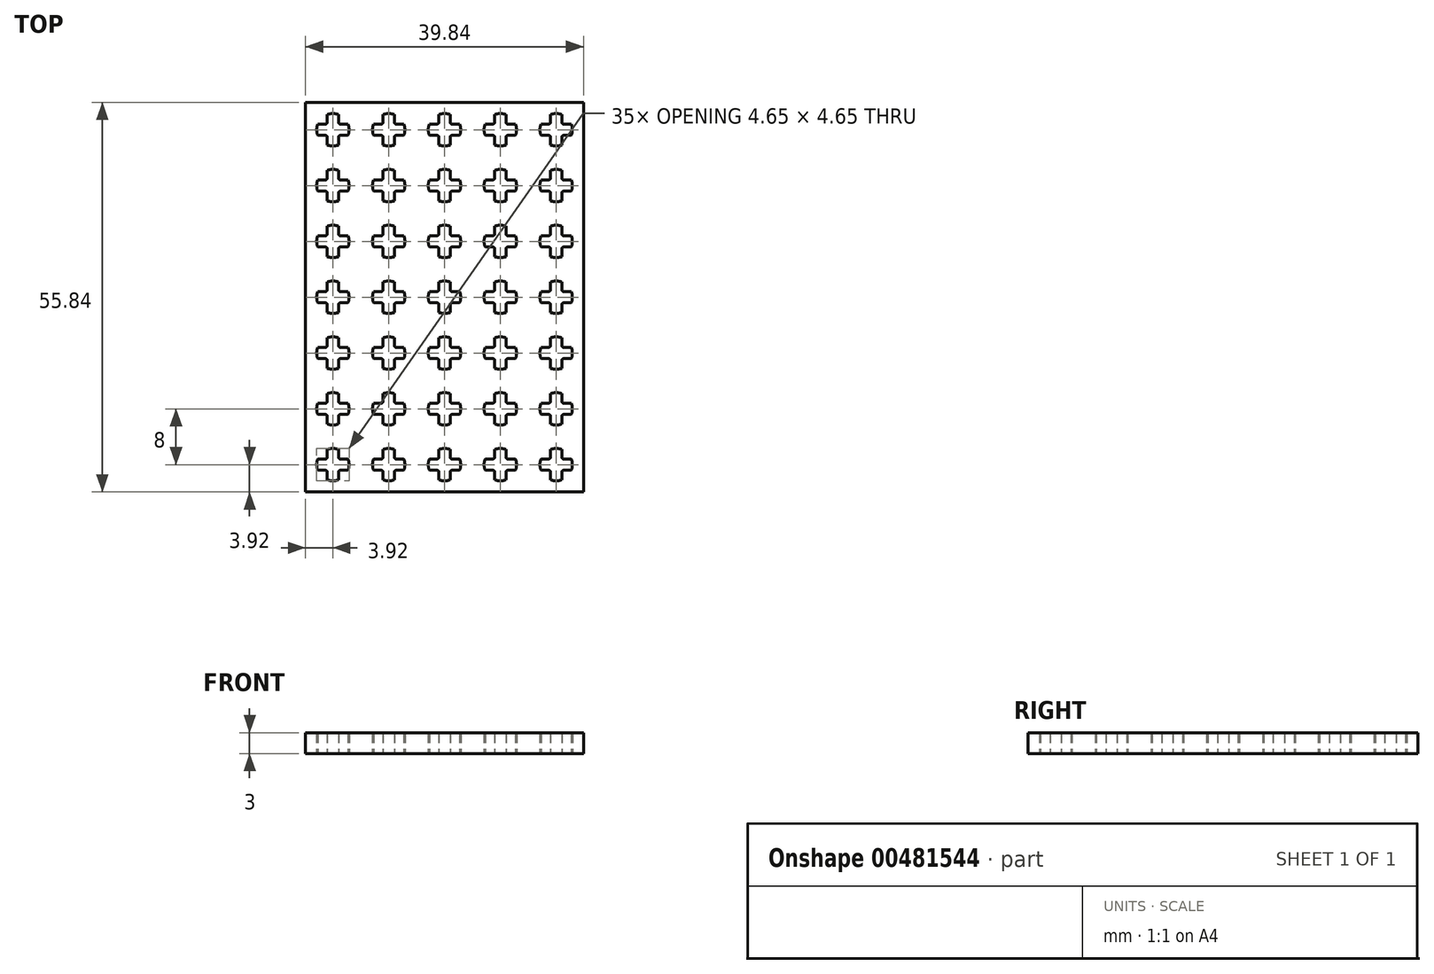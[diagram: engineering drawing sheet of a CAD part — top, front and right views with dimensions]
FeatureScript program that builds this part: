
annotation { "Feature Type Name" : "Feature", "Feature Type Description" : "" }
export const myFeature = defineFeature(function(context is Context, id is Id, definition is map)
    precondition{}
    {
        {
            var Q0;
            Q0=qCreatedBy(makeId("Top.planeOp"),FACE);
            var sketch = newSketch(context, id + "F0", { "sketchPlane" : qUnion([Q0])});
            skLineSegment(sketch, "E0.bottom", {"start": v(-20, 28) * mm, "end": v(20, 28) * mm, "construction": true});
            skLineSegment(sketch, "E0.top", {"start": v(-20, -28) * mm, "end": v(20, -28) * mm, "construction": true});
            skLineSegment(sketch, "E0.left", {"start": v(-20, 28) * mm, "end": v(-20, -28) * mm, "construction": true});
            skLineSegment(sketch, "E0.right", {"start": v(20, 28) * mm, "end": v(20, -28) * mm, "construction": true});
            skLineSegment(sketch, "E1", {"start": v(-16.8, 26.18) * mm, "end": v(-15.2, 26.18) * mm, "construction": true});
            skLineSegment(sketch, "E2", {"start": v(-15.2, 26.18) * mm, "end": v(-15.2, 25.1) * mm});
            skLineSegment(sketch, "E3", {"start": v(-14.9, 24.8) * mm, "end": v(-13.82, 24.8) * mm});
            skLineSegment(sketch, "E4", {"start": v(-13.82, 24.8) * mm, "end": v(-16, 24) * mm, "construction": true});
            skLineSegment(sketch, "E5", {"start": v(-16, 24) * mm, "end": v(-16.8, 26.18) * mm, "construction": true});
            skArc(sketch, "E6", {"start": v(-15.2, 26.18) * mm, "mid": v(-16, 26.33) * mm, "end": v(-16.8, 26.18) * mm});
            skArc(sketch, "E7", {"start": v(-15.2, 25.1) * mm, "mid": v(-15.11, 24.89) * mm, "end": v(-14.9, 24.8) * mm});
            skLineSegment(sketch, "E8", {"start": v(-15.2, 26.18) * mm, "end": v(-15.2, 24.8) * mm, "construction": true});
            skLineSegment(sketch, "E9", {"start": v(-15.2, 24.8) * mm, "end": v(-13.82, 24.8) * mm, "construction": true});
            skArc(sketch, "E10.1.0", {"start": v(-18.18, 24.8) * mm, "mid": v(-18.32, 24) * mm, "end": v(-18.18, 23.2) * mm});
            skArc(sketch, "E10.1.1", {"start": v(-17.1, 24.8) * mm, "mid": v(-16.89, 24.89) * mm, "end": v(-16.8, 25.1) * mm});
            skLineSegment(sketch, "E10.1.2", {"start": v(-18.18, 24.8) * mm, "end": v(-17.1, 24.8) * mm});
            skLineSegment(sketch, "E10.1.3", {"start": v(-16.8, 25.1) * mm, "end": v(-16.8, 26.18) * mm});
            skArc(sketch, "E10.2.0", {"start": v(-16.8, 21.82) * mm, "mid": v(-16, 21.68) * mm, "end": v(-15.2, 21.82) * mm});
            skArc(sketch, "E10.2.1", {"start": v(-16.8, 22.9) * mm, "mid": v(-16.89, 23.11) * mm, "end": v(-17.1, 23.2) * mm});
            skLineSegment(sketch, "E10.2.2", {"start": v(-16.8, 21.82) * mm, "end": v(-16.8, 22.9) * mm});
            skLineSegment(sketch, "E10.2.3", {"start": v(-17.1, 23.2) * mm, "end": v(-18.18, 23.2) * mm});
            skArc(sketch, "E10.3.0", {"start": v(-13.82, 23.2) * mm, "mid": v(-13.67, 24) * mm, "end": v(-13.82, 24.8) * mm});
            skArc(sketch, "E10.3.1", {"start": v(-14.9, 23.2) * mm, "mid": v(-15.11, 23.11) * mm, "end": v(-15.2, 22.9) * mm});
            skLineSegment(sketch, "E10.3.2", {"start": v(-13.82, 23.2) * mm, "end": v(-14.9, 23.2) * mm});
            skLineSegment(sketch, "E10.3.3", {"start": v(-15.2, 22.9) * mm, "end": v(-15.2, 21.82) * mm});
            skLineSegment(sketch, "E11.bottom", {"start": v(-19.92, 27.93) * mm, "end": v(19.93, 27.92) * mm});
            skLineSegment(sketch, "E11.top", {"start": v(-19.93, -27.92) * mm, "end": v(19.92, -27.93) * mm});
            skLineSegment(sketch, "E11.left", {"start": v(-19.92, 27.93) * mm, "end": v(-19.93, -27.92) * mm});
            skLineSegment(sketch, "E11.right", {"start": v(19.93, 27.92) * mm, "end": v(19.92, -27.93) * mm});
            skArc(sketch, "E12.0.1.0", {"start": v(-16.8, 13.82) * mm, "mid": v(-16, 13.67) * mm, "end": v(-15.2, 13.82) * mm});
            skArc(sketch, "E12.0.1.1", {"start": v(-18.18, 16.8) * mm, "mid": v(-18.32, 16) * mm, "end": v(-18.18, 15.2) * mm});
            skArc(sketch, "E12.0.1.2", {"start": v(-15.2, 18.18) * mm, "mid": v(-16, 18.32) * mm, "end": v(-16.8, 18.18) * mm});
            skLineSegment(sketch, "E12.0.1.3", {"start": v(-16.8, 18.18) * mm, "end": v(-15.2, 18.18) * mm, "construction": true});
            skArc(sketch, "E12.0.1.4", {"start": v(-13.82, 15.2) * mm, "mid": v(-13.67, 16) * mm, "end": v(-13.82, 16.8) * mm});
            skPoint(sketch, "E12.0.1.5", {"position": v(-16, 16) * mm});
            skLineSegment(sketch, "E12.0.1.6", {"start": v(-18.18, 16.8) * mm, "end": v(-17.1, 16.8) * mm});
            skLineSegment(sketch, "E12.0.1.7", {"start": v(-17.1, 15.2) * mm, "end": v(-18.18, 15.2) * mm});
            skLineSegment(sketch, "E12.0.1.8", {"start": v(-13.82, 15.2) * mm, "end": v(-14.9, 15.2) * mm});
            skArc(sketch, "E12.0.1.9", {"start": v(-14.9, 15.2) * mm, "mid": v(-15.11, 15.11) * mm, "end": v(-15.2, 14.9) * mm});
            skLineSegment(sketch, "E12.0.1.10", {"start": v(-16, 16) * mm, "end": v(-16.8, 18.18) * mm, "construction": true});
            skLineSegment(sketch, "E12.0.1.11", {"start": v(-16.8, 13.82) * mm, "end": v(-16.8, 14.9) * mm});
            skLineSegment(sketch, "E12.0.1.12", {"start": v(-15.2, 14.9) * mm, "end": v(-15.2, 13.82) * mm});
            skArc(sketch, "E12.0.1.13", {"start": v(-16.8, 14.9) * mm, "mid": v(-16.89, 15.11) * mm, "end": v(-17.1, 15.2) * mm});
            skArc(sketch, "E12.0.1.14", {"start": v(-17.1, 16.8) * mm, "mid": v(-16.89, 16.89) * mm, "end": v(-16.8, 17.1) * mm});
            skLineSegment(sketch, "E12.0.1.15", {"start": v(-16.8, 17.1) * mm, "end": v(-16.8, 18.18) * mm});
            skLineSegment(sketch, "E12.0.1.16", {"start": v(-15.2, 16.8) * mm, "end": v(-13.82, 16.8) * mm, "construction": true});
            skArc(sketch, "E12.0.1.17", {"start": v(-15.2, 17.1) * mm, "mid": v(-15.11, 16.89) * mm, "end": v(-14.9, 16.8) * mm});
            skLineSegment(sketch, "E12.0.1.18", {"start": v(-15.2, 18.18) * mm, "end": v(-15.2, 16.8) * mm, "construction": true});
            skLineSegment(sketch, "E12.0.1.19", {"start": v(-13.82, 16.8) * mm, "end": v(-16, 16) * mm, "construction": true});
            skLineSegment(sketch, "E12.0.1.20", {"start": v(-15.2, 18.18) * mm, "end": v(-15.2, 17.1) * mm});
            skLineSegment(sketch, "E12.0.1.21", {"start": v(-14.9, 16.8) * mm, "end": v(-13.82, 16.8) * mm});
            skArc(sketch, "E12.0.2.0", {"start": v(-16.8, 5.82) * mm, "mid": v(-16, 5.67) * mm, "end": v(-15.2, 5.82) * mm});
            skArc(sketch, "E12.0.2.1", {"start": v(-18.18, 8.8) * mm, "mid": v(-18.32, 8) * mm, "end": v(-18.18, 7.2) * mm});
            skArc(sketch, "E12.0.2.2", {"start": v(-15.2, 10.18) * mm, "mid": v(-16, 10.32) * mm, "end": v(-16.8, 10.18) * mm});
            skLineSegment(sketch, "E12.0.2.3", {"start": v(-16.8, 10.18) * mm, "end": v(-15.2, 10.18) * mm, "construction": true});
            skArc(sketch, "E12.0.2.4", {"start": v(-13.82, 7.2) * mm, "mid": v(-13.67, 8) * mm, "end": v(-13.82, 8.8) * mm});
            skPoint(sketch, "E12.0.2.5", {"position": v(-16, 8) * mm});
            skLineSegment(sketch, "E12.0.2.6", {"start": v(-18.18, 8.8) * mm, "end": v(-17.1, 8.8) * mm});
            skLineSegment(sketch, "E12.0.2.7", {"start": v(-17.1, 7.2) * mm, "end": v(-18.18, 7.2) * mm});
            skLineSegment(sketch, "E12.0.2.8", {"start": v(-13.82, 7.2) * mm, "end": v(-14.9, 7.2) * mm});
            skArc(sketch, "E12.0.2.9", {"start": v(-14.9, 7.2) * mm, "mid": v(-15.11, 7.11) * mm, "end": v(-15.2, 6.9) * mm});
            skLineSegment(sketch, "E12.0.2.10", {"start": v(-16, 8) * mm, "end": v(-16.8, 10.18) * mm, "construction": true});
            skLineSegment(sketch, "E12.0.2.11", {"start": v(-16.8, 5.82) * mm, "end": v(-16.8, 6.9) * mm});
            skLineSegment(sketch, "E12.0.2.12", {"start": v(-15.2, 6.9) * mm, "end": v(-15.2, 5.82) * mm});
            skArc(sketch, "E12.0.2.13", {"start": v(-16.8, 6.9) * mm, "mid": v(-16.89, 7.11) * mm, "end": v(-17.1, 7.2) * mm});
            skArc(sketch, "E12.0.2.14", {"start": v(-17.1, 8.8) * mm, "mid": v(-16.89, 8.89) * mm, "end": v(-16.8, 9.1) * mm});
            skLineSegment(sketch, "E12.0.2.15", {"start": v(-16.8, 9.1) * mm, "end": v(-16.8, 10.18) * mm});
            skLineSegment(sketch, "E12.0.2.16", {"start": v(-15.2, 8.8) * mm, "end": v(-13.82, 8.8) * mm, "construction": true});
            skArc(sketch, "E12.0.2.17", {"start": v(-15.2, 9.1) * mm, "mid": v(-15.11, 8.89) * mm, "end": v(-14.9, 8.8) * mm});
            skLineSegment(sketch, "E12.0.2.18", {"start": v(-15.2, 10.18) * mm, "end": v(-15.2, 8.8) * mm, "construction": true});
            skLineSegment(sketch, "E12.0.2.19", {"start": v(-13.82, 8.8) * mm, "end": v(-16, 8) * mm, "construction": true});
            skLineSegment(sketch, "E12.0.2.20", {"start": v(-15.2, 10.18) * mm, "end": v(-15.2, 9.1) * mm});
            skLineSegment(sketch, "E12.0.2.21", {"start": v(-14.9, 8.8) * mm, "end": v(-13.82, 8.8) * mm});
            skArc(sketch, "E12.0.3.0", {"start": v(-16.8, -2.18) * mm, "mid": v(-16, -2.33) * mm, "end": v(-15.2, -2.18) * mm});
            skArc(sketch, "E12.0.3.1", {"start": v(-18.18, 0.8) * mm, "mid": v(-18.32, 0) * mm, "end": v(-18.18, -0.8) * mm});
            skArc(sketch, "E12.0.3.2", {"start": v(-15.2, 2.18) * mm, "mid": v(-16, 2.32) * mm, "end": v(-16.8, 2.18) * mm});
            skLineSegment(sketch, "E12.0.3.3", {"start": v(-16.8, 2.18) * mm, "end": v(-15.2, 2.18) * mm, "construction": true});
            skArc(sketch, "E12.0.3.4", {"start": v(-13.82, -0.8) * mm, "mid": v(-13.67, 0) * mm, "end": v(-13.82, 0.8) * mm});
            skPoint(sketch, "E12.0.3.5", {"position": v(-16, 0) * mm});
            skLineSegment(sketch, "E12.0.3.6", {"start": v(-18.18, 0.8) * mm, "end": v(-17.1, 0.8) * mm});
            skLineSegment(sketch, "E12.0.3.7", {"start": v(-17.1, -0.8) * mm, "end": v(-18.18, -0.8) * mm});
            skLineSegment(sketch, "E12.0.3.8", {"start": v(-13.82, -0.8) * mm, "end": v(-14.9, -0.8) * mm});
            skArc(sketch, "E12.0.3.9", {"start": v(-14.9, -0.8) * mm, "mid": v(-15.11, -0.89) * mm, "end": v(-15.2, -1.1) * mm});
            skLineSegment(sketch, "E12.0.3.10", {"start": v(-16, 0) * mm, "end": v(-16.8, 2.18) * mm, "construction": true});
            skLineSegment(sketch, "E12.0.3.11", {"start": v(-16.8, -2.18) * mm, "end": v(-16.8, -1.1) * mm});
            skLineSegment(sketch, "E12.0.3.12", {"start": v(-15.2, -1.1) * mm, "end": v(-15.2, -2.18) * mm});
            skArc(sketch, "E12.0.3.13", {"start": v(-16.8, -1.1) * mm, "mid": v(-16.89, -0.89) * mm, "end": v(-17.1, -0.8) * mm});
            skArc(sketch, "E12.0.3.14", {"start": v(-17.1, 0.8) * mm, "mid": v(-16.89, 0.89) * mm, "end": v(-16.8, 1.1) * mm});
            skLineSegment(sketch, "E12.0.3.15", {"start": v(-16.8, 1.1) * mm, "end": v(-16.8, 2.18) * mm});
            skLineSegment(sketch, "E12.0.3.16", {"start": v(-15.2, 0.8) * mm, "end": v(-13.82, 0.8) * mm, "construction": true});
            skArc(sketch, "E12.0.3.17", {"start": v(-15.2, 1.1) * mm, "mid": v(-15.11, 0.89) * mm, "end": v(-14.9, 0.8) * mm});
            skLineSegment(sketch, "E12.0.3.18", {"start": v(-15.2, 2.18) * mm, "end": v(-15.2, 0.8) * mm, "construction": true});
            skLineSegment(sketch, "E12.0.3.19", {"start": v(-13.82, 0.8) * mm, "end": v(-16, 0) * mm, "construction": true});
            skLineSegment(sketch, "E12.0.3.20", {"start": v(-15.2, 2.18) * mm, "end": v(-15.2, 1.1) * mm});
            skLineSegment(sketch, "E12.0.3.21", {"start": v(-14.9, 0.8) * mm, "end": v(-13.82, 0.8) * mm});
            skArc(sketch, "E12.0.4.0", {"start": v(-16.8, -10.18) * mm, "mid": v(-16, -10.33) * mm, "end": v(-15.2, -10.18) * mm});
            skArc(sketch, "E12.0.4.1", {"start": v(-18.18, -7.2) * mm, "mid": v(-18.32, -8) * mm, "end": v(-18.18, -8.8) * mm});
            skArc(sketch, "E12.0.4.2", {"start": v(-15.2, -5.82) * mm, "mid": v(-16, -5.68) * mm, "end": v(-16.8, -5.82) * mm});
            skLineSegment(sketch, "E12.0.4.3", {"start": v(-16.8, -5.82) * mm, "end": v(-15.2, -5.82) * mm, "construction": true});
            skArc(sketch, "E12.0.4.4", {"start": v(-13.82, -8.8) * mm, "mid": v(-13.67, -8) * mm, "end": v(-13.82, -7.2) * mm});
            skPoint(sketch, "E12.0.4.5", {"position": v(-16, -8) * mm});
            skLineSegment(sketch, "E12.0.4.6", {"start": v(-18.18, -7.2) * mm, "end": v(-17.1, -7.2) * mm});
            skLineSegment(sketch, "E12.0.4.7", {"start": v(-17.1, -8.8) * mm, "end": v(-18.18, -8.8) * mm});
            skLineSegment(sketch, "E12.0.4.8", {"start": v(-13.82, -8.8) * mm, "end": v(-14.9, -8.8) * mm});
            skArc(sketch, "E12.0.4.9", {"start": v(-14.9, -8.8) * mm, "mid": v(-15.11, -8.89) * mm, "end": v(-15.2, -9.1) * mm});
            skLineSegment(sketch, "E12.0.4.10", {"start": v(-16, -8) * mm, "end": v(-16.8, -5.82) * mm, "construction": true});
            skLineSegment(sketch, "E12.0.4.11", {"start": v(-16.8, -10.18) * mm, "end": v(-16.8, -9.1) * mm});
            skLineSegment(sketch, "E12.0.4.12", {"start": v(-15.2, -9.1) * mm, "end": v(-15.2, -10.18) * mm});
            skArc(sketch, "E12.0.4.13", {"start": v(-16.8, -9.1) * mm, "mid": v(-16.89, -8.89) * mm, "end": v(-17.1, -8.8) * mm});
            skArc(sketch, "E12.0.4.14", {"start": v(-17.1, -7.2) * mm, "mid": v(-16.89, -7.11) * mm, "end": v(-16.8, -6.9) * mm});
            skLineSegment(sketch, "E12.0.4.15", {"start": v(-16.8, -6.9) * mm, "end": v(-16.8, -5.82) * mm});
            skLineSegment(sketch, "E12.0.4.16", {"start": v(-15.2, -7.2) * mm, "end": v(-13.82, -7.2) * mm, "construction": true});
            skArc(sketch, "E12.0.4.17", {"start": v(-15.2, -6.9) * mm, "mid": v(-15.11, -7.11) * mm, "end": v(-14.9, -7.2) * mm});
            skLineSegment(sketch, "E12.0.4.18", {"start": v(-15.2, -5.82) * mm, "end": v(-15.2, -7.2) * mm, "construction": true});
            skLineSegment(sketch, "E12.0.4.19", {"start": v(-13.82, -7.2) * mm, "end": v(-16, -8) * mm, "construction": true});
            skLineSegment(sketch, "E12.0.4.20", {"start": v(-15.2, -5.82) * mm, "end": v(-15.2, -6.9) * mm});
            skLineSegment(sketch, "E12.0.4.21", {"start": v(-14.9, -7.2) * mm, "end": v(-13.82, -7.2) * mm});
            skArc(sketch, "E12.0.5.0", {"start": v(-16.8, -18.18) * mm, "mid": v(-16, -18.33) * mm, "end": v(-15.2, -18.18) * mm});
            skArc(sketch, "E12.0.5.1", {"start": v(-18.18, -15.2) * mm, "mid": v(-18.32, -16) * mm, "end": v(-18.18, -16.8) * mm});
            skArc(sketch, "E12.0.5.2", {"start": v(-15.2, -13.82) * mm, "mid": v(-16, -13.68) * mm, "end": v(-16.8, -13.82) * mm});
            skLineSegment(sketch, "E12.0.5.3", {"start": v(-16.8, -13.82) * mm, "end": v(-15.2, -13.82) * mm, "construction": true});
            skArc(sketch, "E12.0.5.4", {"start": v(-13.82, -16.8) * mm, "mid": v(-13.67, -16) * mm, "end": v(-13.82, -15.2) * mm});
            skPoint(sketch, "E12.0.5.5", {"position": v(-16, -16) * mm});
            skLineSegment(sketch, "E12.0.5.6", {"start": v(-18.18, -15.2) * mm, "end": v(-17.1, -15.2) * mm});
            skLineSegment(sketch, "E12.0.5.7", {"start": v(-17.1, -16.8) * mm, "end": v(-18.18, -16.8) * mm});
            skLineSegment(sketch, "E12.0.5.8", {"start": v(-13.82, -16.8) * mm, "end": v(-14.9, -16.8) * mm});
            skArc(sketch, "E12.0.5.9", {"start": v(-14.9, -16.8) * mm, "mid": v(-15.11, -16.89) * mm, "end": v(-15.2, -17.1) * mm});
            skLineSegment(sketch, "E12.0.5.10", {"start": v(-16, -16) * mm, "end": v(-16.8, -13.82) * mm, "construction": true});
            skLineSegment(sketch, "E12.0.5.11", {"start": v(-16.8, -18.18) * mm, "end": v(-16.8, -17.1) * mm});
            skLineSegment(sketch, "E12.0.5.12", {"start": v(-15.2, -17.1) * mm, "end": v(-15.2, -18.18) * mm});
            skArc(sketch, "E12.0.5.13", {"start": v(-16.8, -17.1) * mm, "mid": v(-16.89, -16.89) * mm, "end": v(-17.1, -16.8) * mm});
            skArc(sketch, "E12.0.5.14", {"start": v(-17.1, -15.2) * mm, "mid": v(-16.89, -15.11) * mm, "end": v(-16.8, -14.9) * mm});
            skLineSegment(sketch, "E12.0.5.15", {"start": v(-16.8, -14.9) * mm, "end": v(-16.8, -13.82) * mm});
            skLineSegment(sketch, "E12.0.5.16", {"start": v(-15.2, -15.2) * mm, "end": v(-13.82, -15.2) * mm, "construction": true});
            skArc(sketch, "E12.0.5.17", {"start": v(-15.2, -14.9) * mm, "mid": v(-15.11, -15.11) * mm, "end": v(-14.9, -15.2) * mm});
            skLineSegment(sketch, "E12.0.5.18", {"start": v(-15.2, -13.82) * mm, "end": v(-15.2, -15.2) * mm, "construction": true});
            skLineSegment(sketch, "E12.0.5.19", {"start": v(-13.82, -15.2) * mm, "end": v(-16, -16) * mm, "construction": true});
            skLineSegment(sketch, "E12.0.5.20", {"start": v(-15.2, -13.82) * mm, "end": v(-15.2, -14.9) * mm});
            skLineSegment(sketch, "E12.0.5.21", {"start": v(-14.9, -15.2) * mm, "end": v(-13.82, -15.2) * mm});
            skArc(sketch, "E12.0.6.0", {"start": v(-16.8, -26.18) * mm, "mid": v(-16, -26.33) * mm, "end": v(-15.2, -26.18) * mm});
            skArc(sketch, "E12.0.6.1", {"start": v(-18.18, -23.2) * mm, "mid": v(-18.32, -24) * mm, "end": v(-18.18, -24.8) * mm});
            skArc(sketch, "E12.0.6.2", {"start": v(-15.2, -21.82) * mm, "mid": v(-16, -21.68) * mm, "end": v(-16.8, -21.82) * mm});
            skLineSegment(sketch, "E12.0.6.3", {"start": v(-16.8, -21.82) * mm, "end": v(-15.2, -21.82) * mm, "construction": true});
            skArc(sketch, "E12.0.6.4", {"start": v(-13.82, -24.8) * mm, "mid": v(-13.67, -24) * mm, "end": v(-13.82, -23.2) * mm});
            skPoint(sketch, "E12.0.6.5", {"position": v(-16, -24) * mm});
            skLineSegment(sketch, "E12.0.6.6", {"start": v(-18.18, -23.2) * mm, "end": v(-17.1, -23.2) * mm});
            skLineSegment(sketch, "E12.0.6.7", {"start": v(-17.1, -24.8) * mm, "end": v(-18.18, -24.8) * mm});
            skLineSegment(sketch, "E12.0.6.8", {"start": v(-13.82, -24.8) * mm, "end": v(-14.9, -24.8) * mm});
            skArc(sketch, "E12.0.6.9", {"start": v(-14.9, -24.8) * mm, "mid": v(-15.11, -24.89) * mm, "end": v(-15.2, -25.1) * mm});
            skLineSegment(sketch, "E12.0.6.10", {"start": v(-16, -24) * mm, "end": v(-16.8, -21.82) * mm, "construction": true});
            skLineSegment(sketch, "E12.0.6.11", {"start": v(-16.8, -26.18) * mm, "end": v(-16.8, -25.1) * mm});
            skLineSegment(sketch, "E12.0.6.12", {"start": v(-15.2, -25.1) * mm, "end": v(-15.2, -26.18) * mm});
            skArc(sketch, "E12.0.6.13", {"start": v(-16.8, -25.1) * mm, "mid": v(-16.89, -24.89) * mm, "end": v(-17.1, -24.8) * mm});
            skArc(sketch, "E12.0.6.14", {"start": v(-17.1, -23.2) * mm, "mid": v(-16.89, -23.11) * mm, "end": v(-16.8, -22.9) * mm});
            skLineSegment(sketch, "E12.0.6.15", {"start": v(-16.8, -22.9) * mm, "end": v(-16.8, -21.82) * mm});
            skLineSegment(sketch, "E12.0.6.16", {"start": v(-15.2, -23.2) * mm, "end": v(-13.82, -23.2) * mm, "construction": true});
            skArc(sketch, "E12.0.6.17", {"start": v(-15.2, -22.9) * mm, "mid": v(-15.11, -23.11) * mm, "end": v(-14.9, -23.2) * mm});
            skLineSegment(sketch, "E12.0.6.18", {"start": v(-15.2, -21.82) * mm, "end": v(-15.2, -23.2) * mm, "construction": true});
            skLineSegment(sketch, "E12.0.6.19", {"start": v(-13.82, -23.2) * mm, "end": v(-16, -24) * mm, "construction": true});
            skLineSegment(sketch, "E12.0.6.20", {"start": v(-15.2, -21.82) * mm, "end": v(-15.2, -22.9) * mm});
            skLineSegment(sketch, "E12.0.6.21", {"start": v(-14.9, -23.2) * mm, "end": v(-13.82, -23.2) * mm});
            skArc(sketch, "E12.0.7.0", {"start": v(-16.8, -34.18) * mm, "mid": v(-16, -34.33) * mm, "end": v(-15.2, -34.18) * mm});
            skArc(sketch, "E12.0.7.1", {"start": v(-18.18, -31.2) * mm, "mid": v(-18.32, -32) * mm, "end": v(-18.18, -32.8) * mm});
            skArc(sketch, "E12.0.7.2", {"start": v(-15.2, -29.82) * mm, "mid": v(-16, -29.68) * mm, "end": v(-16.8, -29.82) * mm});
            skLineSegment(sketch, "E12.0.7.3", {"start": v(-16.8, -29.82) * mm, "end": v(-15.2, -29.82) * mm, "construction": true});
            skArc(sketch, "E12.0.7.4", {"start": v(-13.82, -32.8) * mm, "mid": v(-13.67, -32) * mm, "end": v(-13.82, -31.2) * mm});
            skPoint(sketch, "E12.0.7.5", {"position": v(-16, -32) * mm});
            skLineSegment(sketch, "E12.0.7.6", {"start": v(-18.18, -31.2) * mm, "end": v(-17.1, -31.2) * mm});
            skLineSegment(sketch, "E12.0.7.7", {"start": v(-17.1, -32.8) * mm, "end": v(-18.18, -32.8) * mm});
            skLineSegment(sketch, "E12.0.7.8", {"start": v(-13.82, -32.8) * mm, "end": v(-14.9, -32.8) * mm});
            skArc(sketch, "E12.0.7.9", {"start": v(-14.9, -32.8) * mm, "mid": v(-15.11, -32.89) * mm, "end": v(-15.2, -33.1) * mm});
            skLineSegment(sketch, "E12.0.7.10", {"start": v(-16, -32) * mm, "end": v(-16.8, -29.82) * mm, "construction": true});
            skLineSegment(sketch, "E12.0.7.11", {"start": v(-16.8, -34.18) * mm, "end": v(-16.8, -33.1) * mm});
            skLineSegment(sketch, "E12.0.7.12", {"start": v(-15.2, -33.1) * mm, "end": v(-15.2, -34.18) * mm});
            skArc(sketch, "E12.0.7.13", {"start": v(-16.8, -33.1) * mm, "mid": v(-16.89, -32.89) * mm, "end": v(-17.1, -32.8) * mm});
            skArc(sketch, "E12.0.7.14", {"start": v(-17.1, -31.2) * mm, "mid": v(-16.89, -31.11) * mm, "end": v(-16.8, -30.9) * mm});
            skLineSegment(sketch, "E12.0.7.15", {"start": v(-16.8, -30.9) * mm, "end": v(-16.8, -29.82) * mm});
            skLineSegment(sketch, "E12.0.7.16", {"start": v(-15.2, -31.2) * mm, "end": v(-13.82, -31.2) * mm, "construction": true});
            skArc(sketch, "E12.0.7.17", {"start": v(-15.2, -30.9) * mm, "mid": v(-15.11, -31.11) * mm, "end": v(-14.9, -31.2) * mm});
            skLineSegment(sketch, "E12.0.7.18", {"start": v(-15.2, -29.82) * mm, "end": v(-15.2, -31.2) * mm, "construction": true});
            skLineSegment(sketch, "E12.0.7.19", {"start": v(-13.82, -31.2) * mm, "end": v(-16, -32) * mm, "construction": true});
            skLineSegment(sketch, "E12.0.7.20", {"start": v(-15.2, -29.82) * mm, "end": v(-15.2, -30.9) * mm});
            skLineSegment(sketch, "E12.0.7.21", {"start": v(-14.9, -31.2) * mm, "end": v(-13.82, -31.2) * mm});
            skArc(sketch, "E12.1.0.0", {"start": v(-8.8, 21.82) * mm, "mid": v(-8, 21.67) * mm, "end": v(-7.2, 21.82) * mm});
            skArc(sketch, "E12.1.0.1", {"start": v(-10.18, 24.8) * mm, "mid": v(-10.33, 24) * mm, "end": v(-10.18, 23.2) * mm});
            skArc(sketch, "E12.1.0.2", {"start": v(-7.2, 26.18) * mm, "mid": v(-8, 26.32) * mm, "end": v(-8.8, 26.18) * mm});
            skLineSegment(sketch, "E12.1.0.3", {"start": v(-8.8, 26.18) * mm, "end": v(-7.2, 26.18) * mm, "construction": true});
            skArc(sketch, "E12.1.0.4", {"start": v(-5.82, 23.2) * mm, "mid": v(-5.67, 24) * mm, "end": v(-5.82, 24.8) * mm});
            skPoint(sketch, "E12.1.0.5", {"position": v(-8, 24) * mm});
            skLineSegment(sketch, "E12.1.0.6", {"start": v(-10.18, 24.8) * mm, "end": v(-9.1, 24.8) * mm});
            skLineSegment(sketch, "E12.1.0.7", {"start": v(-9.1, 23.2) * mm, "end": v(-10.18, 23.2) * mm});
            skLineSegment(sketch, "E12.1.0.8", {"start": v(-5.82, 23.2) * mm, "end": v(-6.9, 23.2) * mm});
            skArc(sketch, "E12.1.0.9", {"start": v(-6.9, 23.2) * mm, "mid": v(-7.11, 23.11) * mm, "end": v(-7.2, 22.9) * mm});
            skLineSegment(sketch, "E12.1.0.10", {"start": v(-8, 24) * mm, "end": v(-8.8, 26.18) * mm, "construction": true});
            skLineSegment(sketch, "E12.1.0.11", {"start": v(-8.8, 21.82) * mm, "end": v(-8.8, 22.9) * mm});
            skLineSegment(sketch, "E12.1.0.12", {"start": v(-7.2, 22.9) * mm, "end": v(-7.2, 21.82) * mm});
            skArc(sketch, "E12.1.0.13", {"start": v(-8.8, 22.9) * mm, "mid": v(-8.89, 23.11) * mm, "end": v(-9.1, 23.2) * mm});
            skArc(sketch, "E12.1.0.14", {"start": v(-9.1, 24.8) * mm, "mid": v(-8.89, 24.89) * mm, "end": v(-8.8, 25.1) * mm});
            skLineSegment(sketch, "E12.1.0.15", {"start": v(-8.8, 25.1) * mm, "end": v(-8.8, 26.18) * mm});
            skLineSegment(sketch, "E12.1.0.16", {"start": v(-7.2, 24.8) * mm, "end": v(-5.82, 24.8) * mm, "construction": true});
            skArc(sketch, "E12.1.0.17", {"start": v(-7.2, 25.1) * mm, "mid": v(-7.11, 24.89) * mm, "end": v(-6.9, 24.8) * mm});
            skLineSegment(sketch, "E12.1.0.18", {"start": v(-7.2, 26.18) * mm, "end": v(-7.2, 24.8) * mm, "construction": true});
            skLineSegment(sketch, "E12.1.0.19", {"start": v(-5.82, 24.8) * mm, "end": v(-8, 24) * mm, "construction": true});
            skLineSegment(sketch, "E12.1.0.20", {"start": v(-7.2, 26.18) * mm, "end": v(-7.2, 25.1) * mm});
            skLineSegment(sketch, "E12.1.0.21", {"start": v(-6.9, 24.8) * mm, "end": v(-5.82, 24.8) * mm});
            skArc(sketch, "E12.1.1.0", {"start": v(-8.8, 13.82) * mm, "mid": v(-8, 13.67) * mm, "end": v(-7.2, 13.82) * mm});
            skArc(sketch, "E12.1.1.1", {"start": v(-10.18, 16.8) * mm, "mid": v(-10.32, 16) * mm, "end": v(-10.18, 15.2) * mm});
            skArc(sketch, "E12.1.1.2", {"start": v(-7.2, 18.18) * mm, "mid": v(-8, 18.32) * mm, "end": v(-8.8, 18.18) * mm});
            skLineSegment(sketch, "E12.1.1.3", {"start": v(-8.8, 18.18) * mm, "end": v(-7.2, 18.18) * mm, "construction": true});
            skArc(sketch, "E12.1.1.4", {"start": v(-5.82, 15.2) * mm, "mid": v(-5.67, 16) * mm, "end": v(-5.82, 16.8) * mm});
            skPoint(sketch, "E12.1.1.5", {"position": v(-8, 16) * mm});
            skLineSegment(sketch, "E12.1.1.6", {"start": v(-10.18, 16.8) * mm, "end": v(-9.1, 16.8) * mm});
            skLineSegment(sketch, "E12.1.1.7", {"start": v(-9.1, 15.2) * mm, "end": v(-10.18, 15.2) * mm});
            skLineSegment(sketch, "E12.1.1.8", {"start": v(-5.82, 15.2) * mm, "end": v(-6.9, 15.2) * mm});
            skArc(sketch, "E12.1.1.9", {"start": v(-6.9, 15.2) * mm, "mid": v(-7.11, 15.11) * mm, "end": v(-7.2, 14.9) * mm});
            skLineSegment(sketch, "E12.1.1.10", {"start": v(-8, 16) * mm, "end": v(-8.8, 18.18) * mm, "construction": true});
            skLineSegment(sketch, "E12.1.1.11", {"start": v(-8.8, 13.82) * mm, "end": v(-8.8, 14.9) * mm});
            skLineSegment(sketch, "E12.1.1.12", {"start": v(-7.2, 14.9) * mm, "end": v(-7.2, 13.82) * mm});
            skArc(sketch, "E12.1.1.13", {"start": v(-8.8, 14.9) * mm, "mid": v(-8.89, 15.11) * mm, "end": v(-9.1, 15.2) * mm});
            skArc(sketch, "E12.1.1.14", {"start": v(-9.1, 16.8) * mm, "mid": v(-8.89, 16.89) * mm, "end": v(-8.8, 17.1) * mm});
            skLineSegment(sketch, "E12.1.1.15", {"start": v(-8.8, 17.1) * mm, "end": v(-8.8, 18.18) * mm});
            skLineSegment(sketch, "E12.1.1.16", {"start": v(-7.2, 16.8) * mm, "end": v(-5.82, 16.8) * mm, "construction": true});
            skArc(sketch, "E12.1.1.17", {"start": v(-7.2, 17.1) * mm, "mid": v(-7.11, 16.89) * mm, "end": v(-6.9, 16.8) * mm});
            skLineSegment(sketch, "E12.1.1.18", {"start": v(-7.2, 18.18) * mm, "end": v(-7.2, 16.8) * mm, "construction": true});
            skLineSegment(sketch, "E12.1.1.19", {"start": v(-5.82, 16.8) * mm, "end": v(-8, 16) * mm, "construction": true});
            skLineSegment(sketch, "E12.1.1.20", {"start": v(-7.2, 18.18) * mm, "end": v(-7.2, 17.1) * mm});
            skLineSegment(sketch, "E12.1.1.21", {"start": v(-6.9, 16.8) * mm, "end": v(-5.82, 16.8) * mm});
            skArc(sketch, "E12.1.2.0", {"start": v(-8.8, 5.82) * mm, "mid": v(-8, 5.67) * mm, "end": v(-7.2, 5.82) * mm});
            skArc(sketch, "E12.1.2.1", {"start": v(-10.18, 8.8) * mm, "mid": v(-10.32, 8) * mm, "end": v(-10.18, 7.2) * mm});
            skArc(sketch, "E12.1.2.2", {"start": v(-7.2, 10.18) * mm, "mid": v(-8, 10.32) * mm, "end": v(-8.8, 10.18) * mm});
            skLineSegment(sketch, "E12.1.2.3", {"start": v(-8.8, 10.18) * mm, "end": v(-7.2, 10.18) * mm, "construction": true});
            skArc(sketch, "E12.1.2.4", {"start": v(-5.82, 7.2) * mm, "mid": v(-5.67, 8) * mm, "end": v(-5.82, 8.8) * mm});
            skPoint(sketch, "E12.1.2.5", {"position": v(-8, 8) * mm});
            skLineSegment(sketch, "E12.1.2.6", {"start": v(-10.18, 8.8) * mm, "end": v(-9.1, 8.8) * mm});
            skLineSegment(sketch, "E12.1.2.7", {"start": v(-9.1, 7.2) * mm, "end": v(-10.18, 7.2) * mm});
            skLineSegment(sketch, "E12.1.2.8", {"start": v(-5.82, 7.2) * mm, "end": v(-6.9, 7.2) * mm});
            skArc(sketch, "E12.1.2.9", {"start": v(-6.9, 7.2) * mm, "mid": v(-7.11, 7.11) * mm, "end": v(-7.2, 6.9) * mm});
            skLineSegment(sketch, "E12.1.2.10", {"start": v(-8, 8) * mm, "end": v(-8.8, 10.18) * mm, "construction": true});
            skLineSegment(sketch, "E12.1.2.11", {"start": v(-8.8, 5.82) * mm, "end": v(-8.8, 6.9) * mm});
            skLineSegment(sketch, "E12.1.2.12", {"start": v(-7.2, 6.9) * mm, "end": v(-7.2, 5.82) * mm});
            skArc(sketch, "E12.1.2.13", {"start": v(-8.8, 6.9) * mm, "mid": v(-8.89, 7.11) * mm, "end": v(-9.1, 7.2) * mm});
            skArc(sketch, "E12.1.2.14", {"start": v(-9.1, 8.8) * mm, "mid": v(-8.89, 8.89) * mm, "end": v(-8.8, 9.1) * mm});
            skLineSegment(sketch, "E12.1.2.15", {"start": v(-8.8, 9.1) * mm, "end": v(-8.8, 10.18) * mm});
            skLineSegment(sketch, "E12.1.2.16", {"start": v(-7.2, 8.8) * mm, "end": v(-5.82, 8.8) * mm, "construction": true});
            skArc(sketch, "E12.1.2.17", {"start": v(-7.2, 9.1) * mm, "mid": v(-7.11, 8.89) * mm, "end": v(-6.9, 8.8) * mm});
            skLineSegment(sketch, "E12.1.2.18", {"start": v(-7.2, 10.18) * mm, "end": v(-7.2, 8.8) * mm, "construction": true});
            skLineSegment(sketch, "E12.1.2.19", {"start": v(-5.82, 8.8) * mm, "end": v(-8, 8) * mm, "construction": true});
            skLineSegment(sketch, "E12.1.2.20", {"start": v(-7.2, 10.18) * mm, "end": v(-7.2, 9.1) * mm});
            skLineSegment(sketch, "E12.1.2.21", {"start": v(-6.9, 8.8) * mm, "end": v(-5.82, 8.8) * mm});
            skArc(sketch, "E12.1.3.0", {"start": v(-8.8, -2.18) * mm, "mid": v(-8, -2.33) * mm, "end": v(-7.2, -2.18) * mm});
            skArc(sketch, "E12.1.3.1", {"start": v(-10.18, 0.8) * mm, "mid": v(-10.32, 0) * mm, "end": v(-10.18, -0.8) * mm});
            skArc(sketch, "E12.1.3.2", {"start": v(-7.2, 2.18) * mm, "mid": v(-8, 2.32) * mm, "end": v(-8.8, 2.18) * mm});
            skLineSegment(sketch, "E12.1.3.3", {"start": v(-8.8, 2.18) * mm, "end": v(-7.2, 2.18) * mm, "construction": true});
            skArc(sketch, "E12.1.3.4", {"start": v(-5.82, -0.8) * mm, "mid": v(-5.67, 0) * mm, "end": v(-5.82, 0.8) * mm});
            skPoint(sketch, "E12.1.3.5", {"position": v(-8, 0) * mm});
            skLineSegment(sketch, "E12.1.3.6", {"start": v(-10.18, 0.8) * mm, "end": v(-9.1, 0.8) * mm});
            skLineSegment(sketch, "E12.1.3.7", {"start": v(-9.1, -0.8) * mm, "end": v(-10.18, -0.8) * mm});
            skLineSegment(sketch, "E12.1.3.8", {"start": v(-5.82, -0.8) * mm, "end": v(-6.9, -0.8) * mm});
            skArc(sketch, "E12.1.3.9", {"start": v(-6.9, -0.8) * mm, "mid": v(-7.11, -0.89) * mm, "end": v(-7.2, -1.1) * mm});
            skLineSegment(sketch, "E12.1.3.10", {"start": v(-8, 0) * mm, "end": v(-8.8, 2.18) * mm, "construction": true});
            skLineSegment(sketch, "E12.1.3.11", {"start": v(-8.8, -2.18) * mm, "end": v(-8.8, -1.1) * mm});
            skLineSegment(sketch, "E12.1.3.12", {"start": v(-7.2, -1.1) * mm, "end": v(-7.2, -2.18) * mm});
            skArc(sketch, "E12.1.3.13", {"start": v(-8.8, -1.1) * mm, "mid": v(-8.89, -0.89) * mm, "end": v(-9.1, -0.8) * mm});
            skArc(sketch, "E12.1.3.14", {"start": v(-9.1, 0.8) * mm, "mid": v(-8.89, 0.89) * mm, "end": v(-8.8, 1.1) * mm});
            skLineSegment(sketch, "E12.1.3.15", {"start": v(-8.8, 1.1) * mm, "end": v(-8.8, 2.18) * mm});
            skLineSegment(sketch, "E12.1.3.16", {"start": v(-7.2, 0.8) * mm, "end": v(-5.82, 0.8) * mm, "construction": true});
            skArc(sketch, "E12.1.3.17", {"start": v(-7.2, 1.1) * mm, "mid": v(-7.11, 0.89) * mm, "end": v(-6.9, 0.8) * mm});
            skLineSegment(sketch, "E12.1.3.18", {"start": v(-7.2, 2.18) * mm, "end": v(-7.2, 0.8) * mm, "construction": true});
            skLineSegment(sketch, "E12.1.3.19", {"start": v(-5.82, 0.8) * mm, "end": v(-8, 0) * mm, "construction": true});
            skLineSegment(sketch, "E12.1.3.20", {"start": v(-7.2, 2.18) * mm, "end": v(-7.2, 1.1) * mm});
            skLineSegment(sketch, "E12.1.3.21", {"start": v(-6.9, 0.8) * mm, "end": v(-5.82, 0.8) * mm});
            skArc(sketch, "E12.1.4.0", {"start": v(-8.8, -10.18) * mm, "mid": v(-8, -10.33) * mm, "end": v(-7.2, -10.18) * mm});
            skArc(sketch, "E12.1.4.1", {"start": v(-10.18, -7.2) * mm, "mid": v(-10.32, -8) * mm, "end": v(-10.18, -8.8) * mm});
            skArc(sketch, "E12.1.4.2", {"start": v(-7.2, -5.82) * mm, "mid": v(-8, -5.68) * mm, "end": v(-8.8, -5.82) * mm});
            skLineSegment(sketch, "E12.1.4.3", {"start": v(-8.8, -5.82) * mm, "end": v(-7.2, -5.82) * mm, "construction": true});
            skArc(sketch, "E12.1.4.4", {"start": v(-5.82, -8.8) * mm, "mid": v(-5.67, -8) * mm, "end": v(-5.82, -7.2) * mm});
            skPoint(sketch, "E12.1.4.5", {"position": v(-8, -8) * mm});
            skLineSegment(sketch, "E12.1.4.6", {"start": v(-10.18, -7.2) * mm, "end": v(-9.1, -7.2) * mm});
            skLineSegment(sketch, "E12.1.4.7", {"start": v(-9.1, -8.8) * mm, "end": v(-10.18, -8.8) * mm});
            skLineSegment(sketch, "E12.1.4.8", {"start": v(-5.82, -8.8) * mm, "end": v(-6.9, -8.8) * mm});
            skArc(sketch, "E12.1.4.9", {"start": v(-6.9, -8.8) * mm, "mid": v(-7.11, -8.89) * mm, "end": v(-7.2, -9.1) * mm});
            skLineSegment(sketch, "E12.1.4.10", {"start": v(-8, -8) * mm, "end": v(-8.8, -5.82) * mm, "construction": true});
            skLineSegment(sketch, "E12.1.4.11", {"start": v(-8.8, -10.18) * mm, "end": v(-8.8, -9.1) * mm});
            skLineSegment(sketch, "E12.1.4.12", {"start": v(-7.2, -9.1) * mm, "end": v(-7.2, -10.18) * mm});
            skArc(sketch, "E12.1.4.13", {"start": v(-8.8, -9.1) * mm, "mid": v(-8.89, -8.89) * mm, "end": v(-9.1, -8.8) * mm});
            skArc(sketch, "E12.1.4.14", {"start": v(-9.1, -7.2) * mm, "mid": v(-8.89, -7.11) * mm, "end": v(-8.8, -6.9) * mm});
            skLineSegment(sketch, "E12.1.4.15", {"start": v(-8.8, -6.9) * mm, "end": v(-8.8, -5.82) * mm});
            skLineSegment(sketch, "E12.1.4.16", {"start": v(-7.2, -7.2) * mm, "end": v(-5.82, -7.2) * mm, "construction": true});
            skArc(sketch, "E12.1.4.17", {"start": v(-7.2, -6.9) * mm, "mid": v(-7.11, -7.11) * mm, "end": v(-6.9, -7.2) * mm});
            skLineSegment(sketch, "E12.1.4.18", {"start": v(-7.2, -5.82) * mm, "end": v(-7.2, -7.2) * mm, "construction": true});
            skLineSegment(sketch, "E12.1.4.19", {"start": v(-5.82, -7.2) * mm, "end": v(-8, -8) * mm, "construction": true});
            skLineSegment(sketch, "E12.1.4.20", {"start": v(-7.2, -5.82) * mm, "end": v(-7.2, -6.9) * mm});
            skLineSegment(sketch, "E12.1.4.21", {"start": v(-6.9, -7.2) * mm, "end": v(-5.82, -7.2) * mm});
            skArc(sketch, "E12.1.5.0", {"start": v(-8.8, -18.18) * mm, "mid": v(-8, -18.33) * mm, "end": v(-7.2, -18.18) * mm});
            skArc(sketch, "E12.1.5.1", {"start": v(-10.18, -15.2) * mm, "mid": v(-10.32, -16) * mm, "end": v(-10.18, -16.8) * mm});
            skArc(sketch, "E12.1.5.2", {"start": v(-7.2, -13.82) * mm, "mid": v(-8, -13.68) * mm, "end": v(-8.8, -13.82) * mm});
            skLineSegment(sketch, "E12.1.5.3", {"start": v(-8.8, -13.82) * mm, "end": v(-7.2, -13.82) * mm, "construction": true});
            skArc(sketch, "E12.1.5.4", {"start": v(-5.82, -16.8) * mm, "mid": v(-5.67, -16) * mm, "end": v(-5.82, -15.2) * mm});
            skPoint(sketch, "E12.1.5.5", {"position": v(-8, -16) * mm});
            skLineSegment(sketch, "E12.1.5.6", {"start": v(-10.18, -15.2) * mm, "end": v(-9.1, -15.2) * mm});
            skLineSegment(sketch, "E12.1.5.7", {"start": v(-9.1, -16.8) * mm, "end": v(-10.18, -16.8) * mm});
            skLineSegment(sketch, "E12.1.5.8", {"start": v(-5.82, -16.8) * mm, "end": v(-6.9, -16.8) * mm});
            skArc(sketch, "E12.1.5.9", {"start": v(-6.9, -16.8) * mm, "mid": v(-7.11, -16.89) * mm, "end": v(-7.2, -17.1) * mm});
            skLineSegment(sketch, "E12.1.5.10", {"start": v(-8, -16) * mm, "end": v(-8.8, -13.82) * mm, "construction": true});
            skLineSegment(sketch, "E12.1.5.11", {"start": v(-8.8, -18.18) * mm, "end": v(-8.8, -17.1) * mm});
            skLineSegment(sketch, "E12.1.5.12", {"start": v(-7.2, -17.1) * mm, "end": v(-7.2, -18.18) * mm});
            skArc(sketch, "E12.1.5.13", {"start": v(-8.8, -17.1) * mm, "mid": v(-8.89, -16.89) * mm, "end": v(-9.1, -16.8) * mm});
            skArc(sketch, "E12.1.5.14", {"start": v(-9.1, -15.2) * mm, "mid": v(-8.89, -15.11) * mm, "end": v(-8.8, -14.9) * mm});
            skLineSegment(sketch, "E12.1.5.15", {"start": v(-8.8, -14.9) * mm, "end": v(-8.8, -13.82) * mm});
            skLineSegment(sketch, "E12.1.5.16", {"start": v(-7.2, -15.2) * mm, "end": v(-5.82, -15.2) * mm, "construction": true});
            skArc(sketch, "E12.1.5.17", {"start": v(-7.2, -14.9) * mm, "mid": v(-7.11, -15.11) * mm, "end": v(-6.9, -15.2) * mm});
            skLineSegment(sketch, "E12.1.5.18", {"start": v(-7.2, -13.82) * mm, "end": v(-7.2, -15.2) * mm, "construction": true});
            skLineSegment(sketch, "E12.1.5.19", {"start": v(-5.82, -15.2) * mm, "end": v(-8, -16) * mm, "construction": true});
            skLineSegment(sketch, "E12.1.5.20", {"start": v(-7.2, -13.82) * mm, "end": v(-7.2, -14.9) * mm});
            skLineSegment(sketch, "E12.1.5.21", {"start": v(-6.9, -15.2) * mm, "end": v(-5.82, -15.2) * mm});
            skArc(sketch, "E12.1.6.0", {"start": v(-8.8, -26.18) * mm, "mid": v(-8, -26.33) * mm, "end": v(-7.2, -26.18) * mm});
            skArc(sketch, "E12.1.6.1", {"start": v(-10.18, -23.2) * mm, "mid": v(-10.32, -24) * mm, "end": v(-10.18, -24.8) * mm});
            skArc(sketch, "E12.1.6.2", {"start": v(-7.2, -21.82) * mm, "mid": v(-8, -21.68) * mm, "end": v(-8.8, -21.82) * mm});
            skLineSegment(sketch, "E12.1.6.3", {"start": v(-8.8, -21.82) * mm, "end": v(-7.2, -21.82) * mm, "construction": true});
            skArc(sketch, "E12.1.6.4", {"start": v(-5.82, -24.8) * mm, "mid": v(-5.67, -24) * mm, "end": v(-5.82, -23.2) * mm});
            skPoint(sketch, "E12.1.6.5", {"position": v(-8, -24) * mm});
            skLineSegment(sketch, "E12.1.6.6", {"start": v(-10.18, -23.2) * mm, "end": v(-9.1, -23.2) * mm});
            skLineSegment(sketch, "E12.1.6.7", {"start": v(-9.1, -24.8) * mm, "end": v(-10.18, -24.8) * mm});
            skLineSegment(sketch, "E12.1.6.8", {"start": v(-5.82, -24.8) * mm, "end": v(-6.9, -24.8) * mm});
            skArc(sketch, "E12.1.6.9", {"start": v(-6.9, -24.8) * mm, "mid": v(-7.11, -24.89) * mm, "end": v(-7.2, -25.1) * mm});
            skLineSegment(sketch, "E12.1.6.10", {"start": v(-8, -24) * mm, "end": v(-8.8, -21.82) * mm, "construction": true});
            skLineSegment(sketch, "E12.1.6.11", {"start": v(-8.8, -26.18) * mm, "end": v(-8.8, -25.1) * mm});
            skLineSegment(sketch, "E12.1.6.12", {"start": v(-7.2, -25.1) * mm, "end": v(-7.2, -26.18) * mm});
            skArc(sketch, "E12.1.6.13", {"start": v(-8.8, -25.1) * mm, "mid": v(-8.89, -24.89) * mm, "end": v(-9.1, -24.8) * mm});
            skArc(sketch, "E12.1.6.14", {"start": v(-9.1, -23.2) * mm, "mid": v(-8.89, -23.11) * mm, "end": v(-8.8, -22.9) * mm});
            skLineSegment(sketch, "E12.1.6.15", {"start": v(-8.8, -22.9) * mm, "end": v(-8.8, -21.82) * mm});
            skLineSegment(sketch, "E12.1.6.16", {"start": v(-7.2, -23.2) * mm, "end": v(-5.82, -23.2) * mm, "construction": true});
            skArc(sketch, "E12.1.6.17", {"start": v(-7.2, -22.9) * mm, "mid": v(-7.11, -23.11) * mm, "end": v(-6.9, -23.2) * mm});
            skLineSegment(sketch, "E12.1.6.18", {"start": v(-7.2, -21.82) * mm, "end": v(-7.2, -23.2) * mm, "construction": true});
            skLineSegment(sketch, "E12.1.6.19", {"start": v(-5.82, -23.2) * mm, "end": v(-8, -24) * mm, "construction": true});
            skLineSegment(sketch, "E12.1.6.20", {"start": v(-7.2, -21.82) * mm, "end": v(-7.2, -22.9) * mm});
            skLineSegment(sketch, "E12.1.6.21", {"start": v(-6.9, -23.2) * mm, "end": v(-5.82, -23.2) * mm});
            skArc(sketch, "E12.1.7.0", {"start": v(-8.8, -34.18) * mm, "mid": v(-8, -34.33) * mm, "end": v(-7.2, -34.18) * mm});
            skArc(sketch, "E12.1.7.1", {"start": v(-10.18, -31.2) * mm, "mid": v(-10.32, -32) * mm, "end": v(-10.18, -32.8) * mm});
            skArc(sketch, "E12.1.7.2", {"start": v(-7.2, -29.82) * mm, "mid": v(-8, -29.68) * mm, "end": v(-8.8, -29.82) * mm});
            skLineSegment(sketch, "E12.1.7.3", {"start": v(-8.8, -29.82) * mm, "end": v(-7.2, -29.82) * mm, "construction": true});
            skArc(sketch, "E12.1.7.4", {"start": v(-5.82, -32.8) * mm, "mid": v(-5.67, -32) * mm, "end": v(-5.82, -31.2) * mm});
            skPoint(sketch, "E12.1.7.5", {"position": v(-8, -32) * mm});
            skLineSegment(sketch, "E12.1.7.6", {"start": v(-10.18, -31.2) * mm, "end": v(-9.1, -31.2) * mm});
            skLineSegment(sketch, "E12.1.7.7", {"start": v(-9.1, -32.8) * mm, "end": v(-10.18, -32.8) * mm});
            skLineSegment(sketch, "E12.1.7.8", {"start": v(-5.82, -32.8) * mm, "end": v(-6.9, -32.8) * mm});
            skArc(sketch, "E12.1.7.9", {"start": v(-6.9, -32.8) * mm, "mid": v(-7.11, -32.89) * mm, "end": v(-7.2, -33.1) * mm});
            skLineSegment(sketch, "E12.1.7.10", {"start": v(-8, -32) * mm, "end": v(-8.8, -29.82) * mm, "construction": true});
            skLineSegment(sketch, "E12.1.7.11", {"start": v(-8.8, -34.18) * mm, "end": v(-8.8, -33.1) * mm});
            skLineSegment(sketch, "E12.1.7.12", {"start": v(-7.2, -33.1) * mm, "end": v(-7.2, -34.18) * mm});
            skArc(sketch, "E12.1.7.13", {"start": v(-8.8, -33.1) * mm, "mid": v(-8.89, -32.89) * mm, "end": v(-9.1, -32.8) * mm});
            skArc(sketch, "E12.1.7.14", {"start": v(-9.1, -31.2) * mm, "mid": v(-8.89, -31.11) * mm, "end": v(-8.8, -30.9) * mm});
            skLineSegment(sketch, "E12.1.7.15", {"start": v(-8.8, -30.9) * mm, "end": v(-8.8, -29.82) * mm});
            skLineSegment(sketch, "E12.1.7.16", {"start": v(-7.2, -31.2) * mm, "end": v(-5.82, -31.2) * mm, "construction": true});
            skArc(sketch, "E12.1.7.17", {"start": v(-7.2, -30.9) * mm, "mid": v(-7.11, -31.11) * mm, "end": v(-6.9, -31.2) * mm});
            skLineSegment(sketch, "E12.1.7.18", {"start": v(-7.2, -29.82) * mm, "end": v(-7.2, -31.2) * mm, "construction": true});
            skLineSegment(sketch, "E12.1.7.19", {"start": v(-5.82, -31.2) * mm, "end": v(-8, -32) * mm, "construction": true});
            skLineSegment(sketch, "E12.1.7.20", {"start": v(-7.2, -29.82) * mm, "end": v(-7.2, -30.9) * mm});
            skLineSegment(sketch, "E12.1.7.21", {"start": v(-6.9, -31.2) * mm, "end": v(-5.82, -31.2) * mm});
            skArc(sketch, "E12.2.0.0", {"start": v(-0.8, 21.82) * mm, "mid": v(0, 21.67) * mm, "end": v(0.8, 21.82) * mm});
            skArc(sketch, "E12.2.0.1", {"start": v(-2.18, 24.8) * mm, "mid": v(-2.33, 24) * mm, "end": v(-2.18, 23.2) * mm});
            skArc(sketch, "E12.2.0.2", {"start": v(0.8, 26.18) * mm, "mid": v(0, 26.32) * mm, "end": v(-0.8, 26.18) * mm});
            skLineSegment(sketch, "E12.2.0.3", {"start": v(-0.8, 26.18) * mm, "end": v(0.8, 26.18) * mm, "construction": true});
            skArc(sketch, "E12.2.0.4", {"start": v(2.18, 23.2) * mm, "mid": v(2.33, 24) * mm, "end": v(2.18, 24.8) * mm});
            skPoint(sketch, "E12.2.0.5", {"position": v(0, 24) * mm});
            skLineSegment(sketch, "E12.2.0.6", {"start": v(-2.18, 24.8) * mm, "end": v(-1.1, 24.8) * mm});
            skLineSegment(sketch, "E12.2.0.7", {"start": v(-1.1, 23.2) * mm, "end": v(-2.18, 23.2) * mm});
            skLineSegment(sketch, "E12.2.0.8", {"start": v(2.18, 23.2) * mm, "end": v(1.1, 23.2) * mm});
            skArc(sketch, "E12.2.0.9", {"start": v(1.1, 23.2) * mm, "mid": v(0.89, 23.11) * mm, "end": v(0.8, 22.9) * mm});
            skLineSegment(sketch, "E12.2.0.10", {"start": v(0, 24) * mm, "end": v(-0.8, 26.18) * mm, "construction": true});
            skLineSegment(sketch, "E12.2.0.11", {"start": v(-0.8, 21.82) * mm, "end": v(-0.8, 22.9) * mm});
            skLineSegment(sketch, "E12.2.0.12", {"start": v(0.8, 22.9) * mm, "end": v(0.8, 21.82) * mm});
            skArc(sketch, "E12.2.0.13", {"start": v(-0.8, 22.9) * mm, "mid": v(-0.89, 23.11) * mm, "end": v(-1.1, 23.2) * mm});
            skArc(sketch, "E12.2.0.14", {"start": v(-1.1, 24.8) * mm, "mid": v(-0.89, 24.89) * mm, "end": v(-0.8, 25.1) * mm});
            skLineSegment(sketch, "E12.2.0.15", {"start": v(-0.8, 25.1) * mm, "end": v(-0.8, 26.18) * mm});
            skLineSegment(sketch, "E12.2.0.16", {"start": v(0.8, 24.8) * mm, "end": v(2.18, 24.8) * mm, "construction": true});
            skArc(sketch, "E12.2.0.17", {"start": v(0.8, 25.1) * mm, "mid": v(0.89, 24.89) * mm, "end": v(1.1, 24.8) * mm});
            skLineSegment(sketch, "E12.2.0.18", {"start": v(0.8, 26.18) * mm, "end": v(0.8, 24.8) * mm, "construction": true});
            skLineSegment(sketch, "E12.2.0.19", {"start": v(2.18, 24.8) * mm, "end": v(0, 24) * mm, "construction": true});
            skLineSegment(sketch, "E12.2.0.20", {"start": v(0.8, 26.18) * mm, "end": v(0.8, 25.1) * mm});
            skLineSegment(sketch, "E12.2.0.21", {"start": v(1.1, 24.8) * mm, "end": v(2.18, 24.8) * mm});
            skArc(sketch, "E12.2.1.0", {"start": v(-0.8, 13.82) * mm, "mid": v(0, 13.67) * mm, "end": v(0.8, 13.82) * mm});
            skArc(sketch, "E12.2.1.1", {"start": v(-2.18, 16.8) * mm, "mid": v(-2.33, 16) * mm, "end": v(-2.18, 15.2) * mm});
            skArc(sketch, "E12.2.1.2", {"start": v(0.8, 18.18) * mm, "mid": v(0, 18.32) * mm, "end": v(-0.8, 18.18) * mm});
            skLineSegment(sketch, "E12.2.1.3", {"start": v(-0.8, 18.18) * mm, "end": v(0.8, 18.18) * mm, "construction": true});
            skArc(sketch, "E12.2.1.4", {"start": v(2.18, 15.2) * mm, "mid": v(2.33, 16) * mm, "end": v(2.18, 16.8) * mm});
            skPoint(sketch, "E12.2.1.5", {"position": v(0, 16) * mm});
            skLineSegment(sketch, "E12.2.1.6", {"start": v(-2.18, 16.8) * mm, "end": v(-1.1, 16.8) * mm});
            skLineSegment(sketch, "E12.2.1.7", {"start": v(-1.1, 15.2) * mm, "end": v(-2.18, 15.2) * mm});
            skLineSegment(sketch, "E12.2.1.8", {"start": v(2.18, 15.2) * mm, "end": v(1.1, 15.2) * mm});
            skArc(sketch, "E12.2.1.9", {"start": v(1.1, 15.2) * mm, "mid": v(0.89, 15.11) * mm, "end": v(0.8, 14.9) * mm});
            skLineSegment(sketch, "E12.2.1.10", {"start": v(0, 16) * mm, "end": v(-0.8, 18.18) * mm, "construction": true});
            skLineSegment(sketch, "E12.2.1.11", {"start": v(-0.8, 13.82) * mm, "end": v(-0.8, 14.9) * mm});
            skLineSegment(sketch, "E12.2.1.12", {"start": v(0.8, 14.9) * mm, "end": v(0.8, 13.82) * mm});
            skArc(sketch, "E12.2.1.13", {"start": v(-0.8, 14.9) * mm, "mid": v(-0.89, 15.11) * mm, "end": v(-1.1, 15.2) * mm});
            skArc(sketch, "E12.2.1.14", {"start": v(-1.1, 16.8) * mm, "mid": v(-0.89, 16.89) * mm, "end": v(-0.8, 17.1) * mm});
            skLineSegment(sketch, "E12.2.1.15", {"start": v(-0.8, 17.1) * mm, "end": v(-0.8, 18.18) * mm});
            skLineSegment(sketch, "E12.2.1.16", {"start": v(0.8, 16.8) * mm, "end": v(2.18, 16.8) * mm, "construction": true});
            skArc(sketch, "E12.2.1.17", {"start": v(0.8, 17.1) * mm, "mid": v(0.89, 16.89) * mm, "end": v(1.1, 16.8) * mm});
            skLineSegment(sketch, "E12.2.1.18", {"start": v(0.8, 18.18) * mm, "end": v(0.8, 16.8) * mm, "construction": true});
            skLineSegment(sketch, "E12.2.1.19", {"start": v(2.18, 16.8) * mm, "end": v(0, 16) * mm, "construction": true});
            skLineSegment(sketch, "E12.2.1.20", {"start": v(0.8, 18.18) * mm, "end": v(0.8, 17.1) * mm});
            skLineSegment(sketch, "E12.2.1.21", {"start": v(1.1, 16.8) * mm, "end": v(2.18, 16.8) * mm});
            skArc(sketch, "E12.2.2.0", {"start": v(-0.8, 5.82) * mm, "mid": v(0, 5.67) * mm, "end": v(0.8, 5.82) * mm});
            skArc(sketch, "E12.2.2.1", {"start": v(-2.18, 8.8) * mm, "mid": v(-2.32, 8) * mm, "end": v(-2.18, 7.2) * mm});
            skArc(sketch, "E12.2.2.2", {"start": v(0.8, 10.18) * mm, "mid": v(0, 10.32) * mm, "end": v(-0.8, 10.18) * mm});
            skLineSegment(sketch, "E12.2.2.3", {"start": v(-0.8, 10.18) * mm, "end": v(0.8, 10.18) * mm, "construction": true});
            skArc(sketch, "E12.2.2.4", {"start": v(2.18, 7.2) * mm, "mid": v(2.33, 8) * mm, "end": v(2.18, 8.8) * mm});
            skPoint(sketch, "E12.2.2.5", {"position": v(0, 8) * mm});
            skLineSegment(sketch, "E12.2.2.6", {"start": v(-2.18, 8.8) * mm, "end": v(-1.1, 8.8) * mm});
            skLineSegment(sketch, "E12.2.2.7", {"start": v(-1.1, 7.2) * mm, "end": v(-2.18, 7.2) * mm});
            skLineSegment(sketch, "E12.2.2.8", {"start": v(2.18, 7.2) * mm, "end": v(1.1, 7.2) * mm});
            skArc(sketch, "E12.2.2.9", {"start": v(1.1, 7.2) * mm, "mid": v(0.89, 7.11) * mm, "end": v(0.8, 6.9) * mm});
            skLineSegment(sketch, "E12.2.2.10", {"start": v(0, 8) * mm, "end": v(-0.8, 10.18) * mm, "construction": true});
            skLineSegment(sketch, "E12.2.2.11", {"start": v(-0.8, 5.82) * mm, "end": v(-0.8, 6.9) * mm});
            skLineSegment(sketch, "E12.2.2.12", {"start": v(0.8, 6.9) * mm, "end": v(0.8, 5.82) * mm});
            skArc(sketch, "E12.2.2.13", {"start": v(-0.8, 6.9) * mm, "mid": v(-0.89, 7.11) * mm, "end": v(-1.1, 7.2) * mm});
            skArc(sketch, "E12.2.2.14", {"start": v(-1.1, 8.8) * mm, "mid": v(-0.89, 8.89) * mm, "end": v(-0.8, 9.1) * mm});
            skLineSegment(sketch, "E12.2.2.15", {"start": v(-0.8, 9.1) * mm, "end": v(-0.8, 10.18) * mm});
            skLineSegment(sketch, "E12.2.2.16", {"start": v(0.8, 8.8) * mm, "end": v(2.18, 8.8) * mm, "construction": true});
            skArc(sketch, "E12.2.2.17", {"start": v(0.8, 9.1) * mm, "mid": v(0.89, 8.89) * mm, "end": v(1.1, 8.8) * mm});
            skLineSegment(sketch, "E12.2.2.18", {"start": v(0.8, 10.18) * mm, "end": v(0.8, 8.8) * mm, "construction": true});
            skLineSegment(sketch, "E12.2.2.19", {"start": v(2.18, 8.8) * mm, "end": v(0, 8) * mm, "construction": true});
            skLineSegment(sketch, "E12.2.2.20", {"start": v(0.8, 10.18) * mm, "end": v(0.8, 9.1) * mm});
            skLineSegment(sketch, "E12.2.2.21", {"start": v(1.1, 8.8) * mm, "end": v(2.18, 8.8) * mm});
            skArc(sketch, "E12.2.3.0", {"start": v(-0.8, -2.18) * mm, "mid": v(0, -2.33) * mm, "end": v(0.8, -2.18) * mm});
            skArc(sketch, "E12.2.3.1", {"start": v(-2.18, 0.8) * mm, "mid": v(-2.32, 0) * mm, "end": v(-2.18, -0.8) * mm});
            skArc(sketch, "E12.2.3.2", {"start": v(0.8, 2.18) * mm, "mid": v(0, 2.32) * mm, "end": v(-0.8, 2.18) * mm});
            skLineSegment(sketch, "E12.2.3.3", {"start": v(-0.8, 2.18) * mm, "end": v(0.8, 2.18) * mm, "construction": true});
            skArc(sketch, "E12.2.3.4", {"start": v(2.18, -0.8) * mm, "mid": v(2.33, 0) * mm, "end": v(2.18, 0.8) * mm});
            skPoint(sketch, "E12.2.3.5", {"position": v(0, 0) * mm});
            skLineSegment(sketch, "E12.2.3.6", {"start": v(-2.18, 0.8) * mm, "end": v(-1.1, 0.8) * mm});
            skLineSegment(sketch, "E12.2.3.7", {"start": v(-1.1, -0.8) * mm, "end": v(-2.18, -0.8) * mm});
            skLineSegment(sketch, "E12.2.3.8", {"start": v(2.18, -0.8) * mm, "end": v(1.1, -0.8) * mm});
            skArc(sketch, "E12.2.3.9", {"start": v(1.1, -0.8) * mm, "mid": v(0.89, -0.89) * mm, "end": v(0.8, -1.1) * mm});
            skLineSegment(sketch, "E12.2.3.10", {"start": v(0, 0) * mm, "end": v(-0.8, 2.18) * mm, "construction": true});
            skLineSegment(sketch, "E12.2.3.11", {"start": v(-0.8, -2.18) * mm, "end": v(-0.8, -1.1) * mm});
            skLineSegment(sketch, "E12.2.3.12", {"start": v(0.8, -1.1) * mm, "end": v(0.8, -2.18) * mm});
            skArc(sketch, "E12.2.3.13", {"start": v(-0.8, -1.1) * mm, "mid": v(-0.89, -0.89) * mm, "end": v(-1.1, -0.8) * mm});
            skArc(sketch, "E12.2.3.14", {"start": v(-1.1, 0.8) * mm, "mid": v(-0.89, 0.89) * mm, "end": v(-0.8, 1.1) * mm});
            skLineSegment(sketch, "E12.2.3.15", {"start": v(-0.8, 1.1) * mm, "end": v(-0.8, 2.18) * mm});
            skLineSegment(sketch, "E12.2.3.16", {"start": v(0.8, 0.8) * mm, "end": v(2.18, 0.8) * mm, "construction": true});
            skArc(sketch, "E12.2.3.17", {"start": v(0.8, 1.1) * mm, "mid": v(0.89, 0.89) * mm, "end": v(1.1, 0.8) * mm});
            skLineSegment(sketch, "E12.2.3.18", {"start": v(0.8, 2.18) * mm, "end": v(0.8, 0.8) * mm, "construction": true});
            skLineSegment(sketch, "E12.2.3.19", {"start": v(2.18, 0.8) * mm, "end": v(0, 0) * mm, "construction": true});
            skLineSegment(sketch, "E12.2.3.20", {"start": v(0.8, 2.18) * mm, "end": v(0.8, 1.1) * mm});
            skLineSegment(sketch, "E12.2.3.21", {"start": v(1.1, 0.8) * mm, "end": v(2.18, 0.8) * mm});
            skArc(sketch, "E12.2.4.0", {"start": v(-0.8, -10.18) * mm, "mid": v(0, -10.33) * mm, "end": v(0.8, -10.18) * mm});
            skArc(sketch, "E12.2.4.1", {"start": v(-2.18, -7.2) * mm, "mid": v(-2.32, -8) * mm, "end": v(-2.18, -8.8) * mm});
            skArc(sketch, "E12.2.4.2", {"start": v(0.8, -5.82) * mm, "mid": v(0, -5.68) * mm, "end": v(-0.8, -5.82) * mm});
            skLineSegment(sketch, "E12.2.4.3", {"start": v(-0.8, -5.82) * mm, "end": v(0.8, -5.82) * mm, "construction": true});
            skArc(sketch, "E12.2.4.4", {"start": v(2.18, -8.8) * mm, "mid": v(2.33, -8) * mm, "end": v(2.18, -7.2) * mm});
            skPoint(sketch, "E12.2.4.5", {"position": v(0, -8) * mm});
            skLineSegment(sketch, "E12.2.4.6", {"start": v(-2.18, -7.2) * mm, "end": v(-1.1, -7.2) * mm});
            skLineSegment(sketch, "E12.2.4.7", {"start": v(-1.1, -8.8) * mm, "end": v(-2.18, -8.8) * mm});
            skLineSegment(sketch, "E12.2.4.8", {"start": v(2.18, -8.8) * mm, "end": v(1.1, -8.8) * mm});
            skArc(sketch, "E12.2.4.9", {"start": v(1.1, -8.8) * mm, "mid": v(0.89, -8.89) * mm, "end": v(0.8, -9.1) * mm});
            skLineSegment(sketch, "E12.2.4.10", {"start": v(0, -8) * mm, "end": v(-0.8, -5.82) * mm, "construction": true});
            skLineSegment(sketch, "E12.2.4.11", {"start": v(-0.8, -10.18) * mm, "end": v(-0.8, -9.1) * mm});
            skLineSegment(sketch, "E12.2.4.12", {"start": v(0.8, -9.1) * mm, "end": v(0.8, -10.18) * mm});
            skArc(sketch, "E12.2.4.13", {"start": v(-0.8, -9.1) * mm, "mid": v(-0.89, -8.89) * mm, "end": v(-1.1, -8.8) * mm});
            skArc(sketch, "E12.2.4.14", {"start": v(-1.1, -7.2) * mm, "mid": v(-0.89, -7.11) * mm, "end": v(-0.8, -6.9) * mm});
            skLineSegment(sketch, "E12.2.4.15", {"start": v(-0.8, -6.9) * mm, "end": v(-0.8, -5.82) * mm});
            skLineSegment(sketch, "E12.2.4.16", {"start": v(0.8, -7.2) * mm, "end": v(2.18, -7.2) * mm, "construction": true});
            skArc(sketch, "E12.2.4.17", {"start": v(0.8, -6.9) * mm, "mid": v(0.89, -7.11) * mm, "end": v(1.1, -7.2) * mm});
            skLineSegment(sketch, "E12.2.4.18", {"start": v(0.8, -5.82) * mm, "end": v(0.8, -7.2) * mm, "construction": true});
            skLineSegment(sketch, "E12.2.4.19", {"start": v(2.18, -7.2) * mm, "end": v(0, -8) * mm, "construction": true});
            skLineSegment(sketch, "E12.2.4.20", {"start": v(0.8, -5.82) * mm, "end": v(0.8, -6.9) * mm});
            skLineSegment(sketch, "E12.2.4.21", {"start": v(1.1, -7.2) * mm, "end": v(2.18, -7.2) * mm});
            skArc(sketch, "E12.2.5.0", {"start": v(-0.8, -18.18) * mm, "mid": v(0, -18.33) * mm, "end": v(0.8, -18.18) * mm});
            skArc(sketch, "E12.2.5.1", {"start": v(-2.18, -15.2) * mm, "mid": v(-2.32, -16) * mm, "end": v(-2.18, -16.8) * mm});
            skArc(sketch, "E12.2.5.2", {"start": v(0.8, -13.82) * mm, "mid": v(0, -13.68) * mm, "end": v(-0.8, -13.82) * mm});
            skLineSegment(sketch, "E12.2.5.3", {"start": v(-0.8, -13.82) * mm, "end": v(0.8, -13.82) * mm, "construction": true});
            skArc(sketch, "E12.2.5.4", {"start": v(2.18, -16.8) * mm, "mid": v(2.33, -16) * mm, "end": v(2.18, -15.2) * mm});
            skPoint(sketch, "E12.2.5.5", {"position": v(0, -16) * mm});
            skLineSegment(sketch, "E12.2.5.6", {"start": v(-2.18, -15.2) * mm, "end": v(-1.1, -15.2) * mm});
            skLineSegment(sketch, "E12.2.5.7", {"start": v(-1.1, -16.8) * mm, "end": v(-2.18, -16.8) * mm});
            skLineSegment(sketch, "E12.2.5.8", {"start": v(2.18, -16.8) * mm, "end": v(1.1, -16.8) * mm});
            skArc(sketch, "E12.2.5.9", {"start": v(1.1, -16.8) * mm, "mid": v(0.89, -16.89) * mm, "end": v(0.8, -17.1) * mm});
            skLineSegment(sketch, "E12.2.5.10", {"start": v(0, -16) * mm, "end": v(-0.8, -13.82) * mm, "construction": true});
            skLineSegment(sketch, "E12.2.5.11", {"start": v(-0.8, -18.18) * mm, "end": v(-0.8, -17.1) * mm});
            skLineSegment(sketch, "E12.2.5.12", {"start": v(0.8, -17.1) * mm, "end": v(0.8, -18.18) * mm});
            skArc(sketch, "E12.2.5.13", {"start": v(-0.8, -17.1) * mm, "mid": v(-0.89, -16.89) * mm, "end": v(-1.1, -16.8) * mm});
            skArc(sketch, "E12.2.5.14", {"start": v(-1.1, -15.2) * mm, "mid": v(-0.89, -15.11) * mm, "end": v(-0.8, -14.9) * mm});
            skLineSegment(sketch, "E12.2.5.15", {"start": v(-0.8, -14.9) * mm, "end": v(-0.8, -13.82) * mm});
            skLineSegment(sketch, "E12.2.5.16", {"start": v(0.8, -15.2) * mm, "end": v(2.18, -15.2) * mm, "construction": true});
            skArc(sketch, "E12.2.5.17", {"start": v(0.8, -14.9) * mm, "mid": v(0.89, -15.11) * mm, "end": v(1.1, -15.2) * mm});
            skLineSegment(sketch, "E12.2.5.18", {"start": v(0.8, -13.82) * mm, "end": v(0.8, -15.2) * mm, "construction": true});
            skLineSegment(sketch, "E12.2.5.19", {"start": v(2.18, -15.2) * mm, "end": v(0, -16) * mm, "construction": true});
            skLineSegment(sketch, "E12.2.5.20", {"start": v(0.8, -13.82) * mm, "end": v(0.8, -14.9) * mm});
            skLineSegment(sketch, "E12.2.5.21", {"start": v(1.1, -15.2) * mm, "end": v(2.18, -15.2) * mm});
            skArc(sketch, "E12.2.6.0", {"start": v(-0.8, -26.18) * mm, "mid": v(0, -26.33) * mm, "end": v(0.8, -26.18) * mm});
            skArc(sketch, "E12.2.6.1", {"start": v(-2.18, -23.2) * mm, "mid": v(-2.32, -24) * mm, "end": v(-2.18, -24.8) * mm});
            skArc(sketch, "E12.2.6.2", {"start": v(0.8, -21.82) * mm, "mid": v(0, -21.68) * mm, "end": v(-0.8, -21.82) * mm});
            skLineSegment(sketch, "E12.2.6.3", {"start": v(-0.8, -21.82) * mm, "end": v(0.8, -21.82) * mm, "construction": true});
            skArc(sketch, "E12.2.6.4", {"start": v(2.18, -24.8) * mm, "mid": v(2.33, -24) * mm, "end": v(2.18, -23.2) * mm});
            skPoint(sketch, "E12.2.6.5", {"position": v(0, -24) * mm});
            skLineSegment(sketch, "E12.2.6.6", {"start": v(-2.18, -23.2) * mm, "end": v(-1.1, -23.2) * mm});
            skLineSegment(sketch, "E12.2.6.7", {"start": v(-1.1, -24.8) * mm, "end": v(-2.18, -24.8) * mm});
            skLineSegment(sketch, "E12.2.6.8", {"start": v(2.18, -24.8) * mm, "end": v(1.1, -24.8) * mm});
            skArc(sketch, "E12.2.6.9", {"start": v(1.1, -24.8) * mm, "mid": v(0.89, -24.89) * mm, "end": v(0.8, -25.1) * mm});
            skLineSegment(sketch, "E12.2.6.10", {"start": v(0, -24) * mm, "end": v(-0.8, -21.82) * mm, "construction": true});
            skLineSegment(sketch, "E12.2.6.11", {"start": v(-0.8, -26.18) * mm, "end": v(-0.8, -25.1) * mm});
            skLineSegment(sketch, "E12.2.6.12", {"start": v(0.8, -25.1) * mm, "end": v(0.8, -26.18) * mm});
            skArc(sketch, "E12.2.6.13", {"start": v(-0.8, -25.1) * mm, "mid": v(-0.89, -24.89) * mm, "end": v(-1.1, -24.8) * mm});
            skArc(sketch, "E12.2.6.14", {"start": v(-1.1, -23.2) * mm, "mid": v(-0.89, -23.11) * mm, "end": v(-0.8, -22.9) * mm});
            skLineSegment(sketch, "E12.2.6.15", {"start": v(-0.8, -22.9) * mm, "end": v(-0.8, -21.82) * mm});
            skLineSegment(sketch, "E12.2.6.16", {"start": v(0.8, -23.2) * mm, "end": v(2.18, -23.2) * mm, "construction": true});
            skArc(sketch, "E12.2.6.17", {"start": v(0.8, -22.9) * mm, "mid": v(0.89, -23.11) * mm, "end": v(1.1, -23.2) * mm});
            skLineSegment(sketch, "E12.2.6.18", {"start": v(0.8, -21.82) * mm, "end": v(0.8, -23.2) * mm, "construction": true});
            skLineSegment(sketch, "E12.2.6.19", {"start": v(2.18, -23.2) * mm, "end": v(0, -24) * mm, "construction": true});
            skLineSegment(sketch, "E12.2.6.20", {"start": v(0.8, -21.82) * mm, "end": v(0.8, -22.9) * mm});
            skLineSegment(sketch, "E12.2.6.21", {"start": v(1.1, -23.2) * mm, "end": v(2.18, -23.2) * mm});
            skArc(sketch, "E12.2.7.0", {"start": v(-0.8, -34.18) * mm, "mid": v(0, -34.33) * mm, "end": v(0.8, -34.18) * mm});
            skArc(sketch, "E12.2.7.1", {"start": v(-2.18, -31.2) * mm, "mid": v(-2.32, -32) * mm, "end": v(-2.18, -32.8) * mm});
            skArc(sketch, "E12.2.7.2", {"start": v(0.8, -29.82) * mm, "mid": v(0, -29.68) * mm, "end": v(-0.8, -29.82) * mm});
            skLineSegment(sketch, "E12.2.7.3", {"start": v(-0.8, -29.82) * mm, "end": v(0.8, -29.82) * mm, "construction": true});
            skArc(sketch, "E12.2.7.4", {"start": v(2.18, -32.8) * mm, "mid": v(2.33, -32) * mm, "end": v(2.18, -31.2) * mm});
            skPoint(sketch, "E12.2.7.5", {"position": v(0, -32) * mm});
            skLineSegment(sketch, "E12.2.7.6", {"start": v(-2.18, -31.2) * mm, "end": v(-1.1, -31.2) * mm});
            skLineSegment(sketch, "E12.2.7.7", {"start": v(-1.1, -32.8) * mm, "end": v(-2.18, -32.8) * mm});
            skLineSegment(sketch, "E12.2.7.8", {"start": v(2.18, -32.8) * mm, "end": v(1.1, -32.8) * mm});
            skArc(sketch, "E12.2.7.9", {"start": v(1.1, -32.8) * mm, "mid": v(0.89, -32.89) * mm, "end": v(0.8, -33.1) * mm});
            skLineSegment(sketch, "E12.2.7.10", {"start": v(0, -32) * mm, "end": v(-0.8, -29.82) * mm, "construction": true});
            skLineSegment(sketch, "E12.2.7.11", {"start": v(-0.8, -34.18) * mm, "end": v(-0.8, -33.1) * mm});
            skLineSegment(sketch, "E12.2.7.12", {"start": v(0.8, -33.1) * mm, "end": v(0.8, -34.18) * mm});
            skArc(sketch, "E12.2.7.13", {"start": v(-0.8, -33.1) * mm, "mid": v(-0.89, -32.89) * mm, "end": v(-1.1, -32.8) * mm});
            skArc(sketch, "E12.2.7.14", {"start": v(-1.1, -31.2) * mm, "mid": v(-0.89, -31.11) * mm, "end": v(-0.8, -30.9) * mm});
            skLineSegment(sketch, "E12.2.7.15", {"start": v(-0.8, -30.9) * mm, "end": v(-0.8, -29.82) * mm});
            skLineSegment(sketch, "E12.2.7.16", {"start": v(0.8, -31.2) * mm, "end": v(2.18, -31.2) * mm, "construction": true});
            skArc(sketch, "E12.2.7.17", {"start": v(0.8, -30.9) * mm, "mid": v(0.89, -31.11) * mm, "end": v(1.1, -31.2) * mm});
            skLineSegment(sketch, "E12.2.7.18", {"start": v(0.8, -29.82) * mm, "end": v(0.8, -31.2) * mm, "construction": true});
            skLineSegment(sketch, "E12.2.7.19", {"start": v(2.18, -31.2) * mm, "end": v(0, -32) * mm, "construction": true});
            skLineSegment(sketch, "E12.2.7.20", {"start": v(0.8, -29.82) * mm, "end": v(0.8, -30.9) * mm});
            skLineSegment(sketch, "E12.2.7.21", {"start": v(1.1, -31.2) * mm, "end": v(2.18, -31.2) * mm});
            skArc(sketch, "E12.3.0.0", {"start": v(7.2, 21.82) * mm, "mid": v(8, 21.67) * mm, "end": v(8.8, 21.82) * mm});
            skArc(sketch, "E12.3.0.1", {"start": v(5.82, 24.8) * mm, "mid": v(5.67, 24) * mm, "end": v(5.82, 23.2) * mm});
            skArc(sketch, "E12.3.0.2", {"start": v(8.8, 26.18) * mm, "mid": v(8, 26.32) * mm, "end": v(7.2, 26.18) * mm});
            skLineSegment(sketch, "E12.3.0.3", {"start": v(7.2, 26.18) * mm, "end": v(8.8, 26.18) * mm, "construction": true});
            skArc(sketch, "E12.3.0.4", {"start": v(10.18, 23.2) * mm, "mid": v(10.33, 24) * mm, "end": v(10.18, 24.8) * mm});
            skPoint(sketch, "E12.3.0.5", {"position": v(8, 24) * mm});
            skLineSegment(sketch, "E12.3.0.6", {"start": v(5.82, 24.8) * mm, "end": v(6.9, 24.8) * mm});
            skLineSegment(sketch, "E12.3.0.7", {"start": v(6.9, 23.2) * mm, "end": v(5.82, 23.2) * mm});
            skLineSegment(sketch, "E12.3.0.8", {"start": v(10.18, 23.2) * mm, "end": v(9.1, 23.2) * mm});
            skArc(sketch, "E12.3.0.9", {"start": v(9.1, 23.2) * mm, "mid": v(8.89, 23.11) * mm, "end": v(8.8, 22.9) * mm});
            skLineSegment(sketch, "E12.3.0.10", {"start": v(8, 24) * mm, "end": v(7.2, 26.18) * mm, "construction": true});
            skLineSegment(sketch, "E12.3.0.11", {"start": v(7.2, 21.82) * mm, "end": v(7.2, 22.9) * mm});
            skLineSegment(sketch, "E12.3.0.12", {"start": v(8.8, 22.9) * mm, "end": v(8.8, 21.82) * mm});
            skArc(sketch, "E12.3.0.13", {"start": v(7.2, 22.9) * mm, "mid": v(7.11, 23.11) * mm, "end": v(6.9, 23.2) * mm});
            skArc(sketch, "E12.3.0.14", {"start": v(6.9, 24.8) * mm, "mid": v(7.11, 24.89) * mm, "end": v(7.2, 25.1) * mm});
            skLineSegment(sketch, "E12.3.0.15", {"start": v(7.2, 25.1) * mm, "end": v(7.2, 26.18) * mm});
            skLineSegment(sketch, "E12.3.0.16", {"start": v(8.8, 24.8) * mm, "end": v(10.18, 24.8) * mm, "construction": true});
            skArc(sketch, "E12.3.0.17", {"start": v(8.8, 25.1) * mm, "mid": v(8.89, 24.89) * mm, "end": v(9.1, 24.8) * mm});
            skLineSegment(sketch, "E12.3.0.18", {"start": v(8.8, 26.18) * mm, "end": v(8.8, 24.8) * mm, "construction": true});
            skLineSegment(sketch, "E12.3.0.19", {"start": v(10.18, 24.8) * mm, "end": v(8, 24) * mm, "construction": true});
            skLineSegment(sketch, "E12.3.0.20", {"start": v(8.8, 26.18) * mm, "end": v(8.8, 25.1) * mm});
            skLineSegment(sketch, "E12.3.0.21", {"start": v(9.1, 24.8) * mm, "end": v(10.18, 24.8) * mm});
            skArc(sketch, "E12.3.1.0", {"start": v(7.2, 13.82) * mm, "mid": v(8, 13.67) * mm, "end": v(8.8, 13.82) * mm});
            skArc(sketch, "E12.3.1.1", {"start": v(5.82, 16.8) * mm, "mid": v(5.67, 16) * mm, "end": v(5.82, 15.2) * mm});
            skArc(sketch, "E12.3.1.2", {"start": v(8.8, 18.18) * mm, "mid": v(8, 18.32) * mm, "end": v(7.2, 18.18) * mm});
            skLineSegment(sketch, "E12.3.1.3", {"start": v(7.2, 18.18) * mm, "end": v(8.8, 18.18) * mm, "construction": true});
            skArc(sketch, "E12.3.1.4", {"start": v(10.18, 15.2) * mm, "mid": v(10.33, 16) * mm, "end": v(10.18, 16.8) * mm});
            skPoint(sketch, "E12.3.1.5", {"position": v(8, 16) * mm});
            skLineSegment(sketch, "E12.3.1.6", {"start": v(5.82, 16.8) * mm, "end": v(6.9, 16.8) * mm});
            skLineSegment(sketch, "E12.3.1.7", {"start": v(6.9, 15.2) * mm, "end": v(5.82, 15.2) * mm});
            skLineSegment(sketch, "E12.3.1.8", {"start": v(10.18, 15.2) * mm, "end": v(9.1, 15.2) * mm});
            skArc(sketch, "E12.3.1.9", {"start": v(9.1, 15.2) * mm, "mid": v(8.89, 15.11) * mm, "end": v(8.8, 14.9) * mm});
            skLineSegment(sketch, "E12.3.1.10", {"start": v(8, 16) * mm, "end": v(7.2, 18.18) * mm, "construction": true});
            skLineSegment(sketch, "E12.3.1.11", {"start": v(7.2, 13.82) * mm, "end": v(7.2, 14.9) * mm});
            skLineSegment(sketch, "E12.3.1.12", {"start": v(8.8, 14.9) * mm, "end": v(8.8, 13.82) * mm});
            skArc(sketch, "E12.3.1.13", {"start": v(7.2, 14.9) * mm, "mid": v(7.11, 15.11) * mm, "end": v(6.9, 15.2) * mm});
            skArc(sketch, "E12.3.1.14", {"start": v(6.9, 16.8) * mm, "mid": v(7.11, 16.89) * mm, "end": v(7.2, 17.1) * mm});
            skLineSegment(sketch, "E12.3.1.15", {"start": v(7.2, 17.1) * mm, "end": v(7.2, 18.18) * mm});
            skLineSegment(sketch, "E12.3.1.16", {"start": v(8.8, 16.8) * mm, "end": v(10.18, 16.8) * mm, "construction": true});
            skArc(sketch, "E12.3.1.17", {"start": v(8.8, 17.1) * mm, "mid": v(8.89, 16.89) * mm, "end": v(9.1, 16.8) * mm});
            skLineSegment(sketch, "E12.3.1.18", {"start": v(8.8, 18.18) * mm, "end": v(8.8, 16.8) * mm, "construction": true});
            skLineSegment(sketch, "E12.3.1.19", {"start": v(10.18, 16.8) * mm, "end": v(8, 16) * mm, "construction": true});
            skLineSegment(sketch, "E12.3.1.20", {"start": v(8.8, 18.18) * mm, "end": v(8.8, 17.1) * mm});
            skLineSegment(sketch, "E12.3.1.21", {"start": v(9.1, 16.8) * mm, "end": v(10.18, 16.8) * mm});
            skArc(sketch, "E12.3.2.0", {"start": v(7.2, 5.82) * mm, "mid": v(8, 5.67) * mm, "end": v(8.8, 5.82) * mm});
            skArc(sketch, "E12.3.2.1", {"start": v(5.82, 8.8) * mm, "mid": v(5.68, 8) * mm, "end": v(5.82, 7.2) * mm});
            skArc(sketch, "E12.3.2.2", {"start": v(8.8, 10.18) * mm, "mid": v(8, 10.32) * mm, "end": v(7.2, 10.18) * mm});
            skLineSegment(sketch, "E12.3.2.3", {"start": v(7.2, 10.18) * mm, "end": v(8.8, 10.18) * mm, "construction": true});
            skArc(sketch, "E12.3.2.4", {"start": v(10.18, 7.2) * mm, "mid": v(10.33, 8) * mm, "end": v(10.18, 8.8) * mm});
            skPoint(sketch, "E12.3.2.5", {"position": v(8, 8) * mm});
            skLineSegment(sketch, "E12.3.2.6", {"start": v(5.82, 8.8) * mm, "end": v(6.9, 8.8) * mm});
            skLineSegment(sketch, "E12.3.2.7", {"start": v(6.9, 7.2) * mm, "end": v(5.82, 7.2) * mm});
            skLineSegment(sketch, "E12.3.2.8", {"start": v(10.18, 7.2) * mm, "end": v(9.1, 7.2) * mm});
            skArc(sketch, "E12.3.2.9", {"start": v(9.1, 7.2) * mm, "mid": v(8.89, 7.11) * mm, "end": v(8.8, 6.9) * mm});
            skLineSegment(sketch, "E12.3.2.10", {"start": v(8, 8) * mm, "end": v(7.2, 10.18) * mm, "construction": true});
            skLineSegment(sketch, "E12.3.2.11", {"start": v(7.2, 5.82) * mm, "end": v(7.2, 6.9) * mm});
            skLineSegment(sketch, "E12.3.2.12", {"start": v(8.8, 6.9) * mm, "end": v(8.8, 5.82) * mm});
            skArc(sketch, "E12.3.2.13", {"start": v(7.2, 6.9) * mm, "mid": v(7.11, 7.11) * mm, "end": v(6.9, 7.2) * mm});
            skArc(sketch, "E12.3.2.14", {"start": v(6.9, 8.8) * mm, "mid": v(7.11, 8.89) * mm, "end": v(7.2, 9.1) * mm});
            skLineSegment(sketch, "E12.3.2.15", {"start": v(7.2, 9.1) * mm, "end": v(7.2, 10.18) * mm});
            skLineSegment(sketch, "E12.3.2.16", {"start": v(8.8, 8.8) * mm, "end": v(10.18, 8.8) * mm, "construction": true});
            skArc(sketch, "E12.3.2.17", {"start": v(8.8, 9.1) * mm, "mid": v(8.89, 8.89) * mm, "end": v(9.1, 8.8) * mm});
            skLineSegment(sketch, "E12.3.2.18", {"start": v(8.8, 10.18) * mm, "end": v(8.8, 8.8) * mm, "construction": true});
            skLineSegment(sketch, "E12.3.2.19", {"start": v(10.18, 8.8) * mm, "end": v(8, 8) * mm, "construction": true});
            skLineSegment(sketch, "E12.3.2.20", {"start": v(8.8, 10.18) * mm, "end": v(8.8, 9.1) * mm});
            skLineSegment(sketch, "E12.3.2.21", {"start": v(9.1, 8.8) * mm, "end": v(10.18, 8.8) * mm});
            skArc(sketch, "E12.3.3.0", {"start": v(7.2, -2.18) * mm, "mid": v(8, -2.33) * mm, "end": v(8.8, -2.18) * mm});
            skArc(sketch, "E12.3.3.1", {"start": v(5.82, 0.8) * mm, "mid": v(5.68, 0) * mm, "end": v(5.82, -0.8) * mm});
            skArc(sketch, "E12.3.3.2", {"start": v(8.8, 2.18) * mm, "mid": v(8, 2.32) * mm, "end": v(7.2, 2.18) * mm});
            skLineSegment(sketch, "E12.3.3.3", {"start": v(7.2, 2.18) * mm, "end": v(8.8, 2.18) * mm, "construction": true});
            skArc(sketch, "E12.3.3.4", {"start": v(10.18, -0.8) * mm, "mid": v(10.33, 0) * mm, "end": v(10.18, 0.8) * mm});
            skPoint(sketch, "E12.3.3.5", {"position": v(8, 0) * mm});
            skLineSegment(sketch, "E12.3.3.6", {"start": v(5.82, 0.8) * mm, "end": v(6.9, 0.8) * mm});
            skLineSegment(sketch, "E12.3.3.7", {"start": v(6.9, -0.8) * mm, "end": v(5.82, -0.8) * mm});
            skLineSegment(sketch, "E12.3.3.8", {"start": v(10.18, -0.8) * mm, "end": v(9.1, -0.8) * mm});
            skArc(sketch, "E12.3.3.9", {"start": v(9.1, -0.8) * mm, "mid": v(8.89, -0.89) * mm, "end": v(8.8, -1.1) * mm});
            skLineSegment(sketch, "E12.3.3.10", {"start": v(8, 0) * mm, "end": v(7.2, 2.18) * mm, "construction": true});
            skLineSegment(sketch, "E12.3.3.11", {"start": v(7.2, -2.18) * mm, "end": v(7.2, -1.1) * mm});
            skLineSegment(sketch, "E12.3.3.12", {"start": v(8.8, -1.1) * mm, "end": v(8.8, -2.18) * mm});
            skArc(sketch, "E12.3.3.13", {"start": v(7.2, -1.1) * mm, "mid": v(7.11, -0.89) * mm, "end": v(6.9, -0.8) * mm});
            skArc(sketch, "E12.3.3.14", {"start": v(6.9, 0.8) * mm, "mid": v(7.11, 0.89) * mm, "end": v(7.2, 1.1) * mm});
            skLineSegment(sketch, "E12.3.3.15", {"start": v(7.2, 1.1) * mm, "end": v(7.2, 2.18) * mm});
            skLineSegment(sketch, "E12.3.3.16", {"start": v(8.8, 0.8) * mm, "end": v(10.18, 0.8) * mm, "construction": true});
            skArc(sketch, "E12.3.3.17", {"start": v(8.8, 1.1) * mm, "mid": v(8.89, 0.89) * mm, "end": v(9.1, 0.8) * mm});
            skLineSegment(sketch, "E12.3.3.18", {"start": v(8.8, 2.18) * mm, "end": v(8.8, 0.8) * mm, "construction": true});
            skLineSegment(sketch, "E12.3.3.19", {"start": v(10.18, 0.8) * mm, "end": v(8, 0) * mm, "construction": true});
            skLineSegment(sketch, "E12.3.3.20", {"start": v(8.8, 2.18) * mm, "end": v(8.8, 1.1) * mm});
            skLineSegment(sketch, "E12.3.3.21", {"start": v(9.1, 0.8) * mm, "end": v(10.18, 0.8) * mm});
            skArc(sketch, "E12.3.4.0", {"start": v(7.2, -10.18) * mm, "mid": v(8, -10.33) * mm, "end": v(8.8, -10.18) * mm});
            skArc(sketch, "E12.3.4.1", {"start": v(5.82, -7.2) * mm, "mid": v(5.68, -8) * mm, "end": v(5.82, -8.8) * mm});
            skArc(sketch, "E12.3.4.2", {"start": v(8.8, -5.82) * mm, "mid": v(8, -5.68) * mm, "end": v(7.2, -5.82) * mm});
            skLineSegment(sketch, "E12.3.4.3", {"start": v(7.2, -5.82) * mm, "end": v(8.8, -5.82) * mm, "construction": true});
            skArc(sketch, "E12.3.4.4", {"start": v(10.18, -8.8) * mm, "mid": v(10.33, -8) * mm, "end": v(10.18, -7.2) * mm});
            skPoint(sketch, "E12.3.4.5", {"position": v(8, -8) * mm});
            skLineSegment(sketch, "E12.3.4.6", {"start": v(5.82, -7.2) * mm, "end": v(6.9, -7.2) * mm});
            skLineSegment(sketch, "E12.3.4.7", {"start": v(6.9, -8.8) * mm, "end": v(5.82, -8.8) * mm});
            skLineSegment(sketch, "E12.3.4.8", {"start": v(10.18, -8.8) * mm, "end": v(9.1, -8.8) * mm});
            skArc(sketch, "E12.3.4.9", {"start": v(9.1, -8.8) * mm, "mid": v(8.89, -8.89) * mm, "end": v(8.8, -9.1) * mm});
            skLineSegment(sketch, "E12.3.4.10", {"start": v(8, -8) * mm, "end": v(7.2, -5.82) * mm, "construction": true});
            skLineSegment(sketch, "E12.3.4.11", {"start": v(7.2, -10.18) * mm, "end": v(7.2, -9.1) * mm});
            skLineSegment(sketch, "E12.3.4.12", {"start": v(8.8, -9.1) * mm, "end": v(8.8, -10.18) * mm});
            skArc(sketch, "E12.3.4.13", {"start": v(7.2, -9.1) * mm, "mid": v(7.11, -8.89) * mm, "end": v(6.9, -8.8) * mm});
            skArc(sketch, "E12.3.4.14", {"start": v(6.9, -7.2) * mm, "mid": v(7.11, -7.11) * mm, "end": v(7.2, -6.9) * mm});
            skLineSegment(sketch, "E12.3.4.15", {"start": v(7.2, -6.9) * mm, "end": v(7.2, -5.82) * mm});
            skLineSegment(sketch, "E12.3.4.16", {"start": v(8.8, -7.2) * mm, "end": v(10.18, -7.2) * mm, "construction": true});
            skArc(sketch, "E12.3.4.17", {"start": v(8.8, -6.9) * mm, "mid": v(8.89, -7.11) * mm, "end": v(9.1, -7.2) * mm});
            skLineSegment(sketch, "E12.3.4.18", {"start": v(8.8, -5.82) * mm, "end": v(8.8, -7.2) * mm, "construction": true});
            skLineSegment(sketch, "E12.3.4.19", {"start": v(10.18, -7.2) * mm, "end": v(8, -8) * mm, "construction": true});
            skLineSegment(sketch, "E12.3.4.20", {"start": v(8.8, -5.82) * mm, "end": v(8.8, -6.9) * mm});
            skLineSegment(sketch, "E12.3.4.21", {"start": v(9.1, -7.2) * mm, "end": v(10.18, -7.2) * mm});
            skArc(sketch, "E12.3.5.0", {"start": v(7.2, -18.18) * mm, "mid": v(8, -18.33) * mm, "end": v(8.8, -18.18) * mm});
            skArc(sketch, "E12.3.5.1", {"start": v(5.82, -15.2) * mm, "mid": v(5.68, -16) * mm, "end": v(5.82, -16.8) * mm});
            skArc(sketch, "E12.3.5.2", {"start": v(8.8, -13.82) * mm, "mid": v(8, -13.68) * mm, "end": v(7.2, -13.82) * mm});
            skLineSegment(sketch, "E12.3.5.3", {"start": v(7.2, -13.82) * mm, "end": v(8.8, -13.82) * mm, "construction": true});
            skArc(sketch, "E12.3.5.4", {"start": v(10.18, -16.8) * mm, "mid": v(10.33, -16) * mm, "end": v(10.18, -15.2) * mm});
            skPoint(sketch, "E12.3.5.5", {"position": v(8, -16) * mm});
            skLineSegment(sketch, "E12.3.5.6", {"start": v(5.82, -15.2) * mm, "end": v(6.9, -15.2) * mm});
            skLineSegment(sketch, "E12.3.5.7", {"start": v(6.9, -16.8) * mm, "end": v(5.82, -16.8) * mm});
            skLineSegment(sketch, "E12.3.5.8", {"start": v(10.18, -16.8) * mm, "end": v(9.1, -16.8) * mm});
            skArc(sketch, "E12.3.5.9", {"start": v(9.1, -16.8) * mm, "mid": v(8.89, -16.89) * mm, "end": v(8.8, -17.1) * mm});
            skLineSegment(sketch, "E12.3.5.10", {"start": v(8, -16) * mm, "end": v(7.2, -13.82) * mm, "construction": true});
            skLineSegment(sketch, "E12.3.5.11", {"start": v(7.2, -18.18) * mm, "end": v(7.2, -17.1) * mm});
            skLineSegment(sketch, "E12.3.5.12", {"start": v(8.8, -17.1) * mm, "end": v(8.8, -18.18) * mm});
            skArc(sketch, "E12.3.5.13", {"start": v(7.2, -17.1) * mm, "mid": v(7.11, -16.89) * mm, "end": v(6.9, -16.8) * mm});
            skArc(sketch, "E12.3.5.14", {"start": v(6.9, -15.2) * mm, "mid": v(7.11, -15.11) * mm, "end": v(7.2, -14.9) * mm});
            skLineSegment(sketch, "E12.3.5.15", {"start": v(7.2, -14.9) * mm, "end": v(7.2, -13.82) * mm});
            skLineSegment(sketch, "E12.3.5.16", {"start": v(8.8, -15.2) * mm, "end": v(10.18, -15.2) * mm, "construction": true});
            skArc(sketch, "E12.3.5.17", {"start": v(8.8, -14.9) * mm, "mid": v(8.89, -15.11) * mm, "end": v(9.1, -15.2) * mm});
            skLineSegment(sketch, "E12.3.5.18", {"start": v(8.8, -13.82) * mm, "end": v(8.8, -15.2) * mm, "construction": true});
            skLineSegment(sketch, "E12.3.5.19", {"start": v(10.18, -15.2) * mm, "end": v(8, -16) * mm, "construction": true});
            skLineSegment(sketch, "E12.3.5.20", {"start": v(8.8, -13.82) * mm, "end": v(8.8, -14.9) * mm});
            skLineSegment(sketch, "E12.3.5.21", {"start": v(9.1, -15.2) * mm, "end": v(10.18, -15.2) * mm});
            skArc(sketch, "E12.3.6.0", {"start": v(7.2, -26.18) * mm, "mid": v(8, -26.33) * mm, "end": v(8.8, -26.18) * mm});
            skArc(sketch, "E12.3.6.1", {"start": v(5.82, -23.2) * mm, "mid": v(5.68, -24) * mm, "end": v(5.82, -24.8) * mm});
            skArc(sketch, "E12.3.6.2", {"start": v(8.8, -21.82) * mm, "mid": v(8, -21.68) * mm, "end": v(7.2, -21.82) * mm});
            skLineSegment(sketch, "E12.3.6.3", {"start": v(7.2, -21.82) * mm, "end": v(8.8, -21.82) * mm, "construction": true});
            skArc(sketch, "E12.3.6.4", {"start": v(10.18, -24.8) * mm, "mid": v(10.33, -24) * mm, "end": v(10.18, -23.2) * mm});
            skPoint(sketch, "E12.3.6.5", {"position": v(8, -24) * mm});
            skLineSegment(sketch, "E12.3.6.6", {"start": v(5.82, -23.2) * mm, "end": v(6.9, -23.2) * mm});
            skLineSegment(sketch, "E12.3.6.7", {"start": v(6.9, -24.8) * mm, "end": v(5.82, -24.8) * mm});
            skLineSegment(sketch, "E12.3.6.8", {"start": v(10.18, -24.8) * mm, "end": v(9.1, -24.8) * mm});
            skArc(sketch, "E12.3.6.9", {"start": v(9.1, -24.8) * mm, "mid": v(8.89, -24.89) * mm, "end": v(8.8, -25.1) * mm});
            skLineSegment(sketch, "E12.3.6.10", {"start": v(8, -24) * mm, "end": v(7.2, -21.82) * mm, "construction": true});
            skLineSegment(sketch, "E12.3.6.11", {"start": v(7.2, -26.18) * mm, "end": v(7.2, -25.1) * mm});
            skLineSegment(sketch, "E12.3.6.12", {"start": v(8.8, -25.1) * mm, "end": v(8.8, -26.18) * mm});
            skArc(sketch, "E12.3.6.13", {"start": v(7.2, -25.1) * mm, "mid": v(7.11, -24.89) * mm, "end": v(6.9, -24.8) * mm});
            skArc(sketch, "E12.3.6.14", {"start": v(6.9, -23.2) * mm, "mid": v(7.11, -23.11) * mm, "end": v(7.2, -22.9) * mm});
            skLineSegment(sketch, "E12.3.6.15", {"start": v(7.2, -22.9) * mm, "end": v(7.2, -21.82) * mm});
            skLineSegment(sketch, "E12.3.6.16", {"start": v(8.8, -23.2) * mm, "end": v(10.18, -23.2) * mm, "construction": true});
            skArc(sketch, "E12.3.6.17", {"start": v(8.8, -22.9) * mm, "mid": v(8.89, -23.11) * mm, "end": v(9.1, -23.2) * mm});
            skLineSegment(sketch, "E12.3.6.18", {"start": v(8.8, -21.82) * mm, "end": v(8.8, -23.2) * mm, "construction": true});
            skLineSegment(sketch, "E12.3.6.19", {"start": v(10.18, -23.2) * mm, "end": v(8, -24) * mm, "construction": true});
            skLineSegment(sketch, "E12.3.6.20", {"start": v(8.8, -21.82) * mm, "end": v(8.8, -22.9) * mm});
            skLineSegment(sketch, "E12.3.6.21", {"start": v(9.1, -23.2) * mm, "end": v(10.18, -23.2) * mm});
            skArc(sketch, "E12.3.7.0", {"start": v(7.2, -34.18) * mm, "mid": v(8, -34.33) * mm, "end": v(8.8, -34.18) * mm});
            skArc(sketch, "E12.3.7.1", {"start": v(5.82, -31.2) * mm, "mid": v(5.68, -32) * mm, "end": v(5.82, -32.8) * mm});
            skArc(sketch, "E12.3.7.2", {"start": v(8.8, -29.82) * mm, "mid": v(8, -29.68) * mm, "end": v(7.2, -29.82) * mm});
            skLineSegment(sketch, "E12.3.7.3", {"start": v(7.2, -29.82) * mm, "end": v(8.8, -29.82) * mm, "construction": true});
            skArc(sketch, "E12.3.7.4", {"start": v(10.18, -32.8) * mm, "mid": v(10.33, -32) * mm, "end": v(10.18, -31.2) * mm});
            skPoint(sketch, "E12.3.7.5", {"position": v(8, -32) * mm});
            skLineSegment(sketch, "E12.3.7.6", {"start": v(5.82, -31.2) * mm, "end": v(6.9, -31.2) * mm});
            skLineSegment(sketch, "E12.3.7.7", {"start": v(6.9, -32.8) * mm, "end": v(5.82, -32.8) * mm});
            skLineSegment(sketch, "E12.3.7.8", {"start": v(10.18, -32.8) * mm, "end": v(9.1, -32.8) * mm});
            skArc(sketch, "E12.3.7.9", {"start": v(9.1, -32.8) * mm, "mid": v(8.89, -32.89) * mm, "end": v(8.8, -33.1) * mm});
            skLineSegment(sketch, "E12.3.7.10", {"start": v(8, -32) * mm, "end": v(7.2, -29.82) * mm, "construction": true});
            skLineSegment(sketch, "E12.3.7.11", {"start": v(7.2, -34.18) * mm, "end": v(7.2, -33.1) * mm});
            skLineSegment(sketch, "E12.3.7.12", {"start": v(8.8, -33.1) * mm, "end": v(8.8, -34.18) * mm});
            skArc(sketch, "E12.3.7.13", {"start": v(7.2, -33.1) * mm, "mid": v(7.11, -32.89) * mm, "end": v(6.9, -32.8) * mm});
            skArc(sketch, "E12.3.7.14", {"start": v(6.9, -31.2) * mm, "mid": v(7.11, -31.11) * mm, "end": v(7.2, -30.9) * mm});
            skLineSegment(sketch, "E12.3.7.15", {"start": v(7.2, -30.9) * mm, "end": v(7.2, -29.82) * mm});
            skLineSegment(sketch, "E12.3.7.16", {"start": v(8.8, -31.2) * mm, "end": v(10.18, -31.2) * mm, "construction": true});
            skArc(sketch, "E12.3.7.17", {"start": v(8.8, -30.9) * mm, "mid": v(8.89, -31.11) * mm, "end": v(9.1, -31.2) * mm});
            skLineSegment(sketch, "E12.3.7.18", {"start": v(8.8, -29.82) * mm, "end": v(8.8, -31.2) * mm, "construction": true});
            skLineSegment(sketch, "E12.3.7.19", {"start": v(10.18, -31.2) * mm, "end": v(8, -32) * mm, "construction": true});
            skLineSegment(sketch, "E12.3.7.20", {"start": v(8.8, -29.82) * mm, "end": v(8.8, -30.9) * mm});
            skLineSegment(sketch, "E12.3.7.21", {"start": v(9.1, -31.2) * mm, "end": v(10.18, -31.2) * mm});
            skArc(sketch, "E12.4.0.0", {"start": v(15.2, 21.82) * mm, "mid": v(16, 21.67) * mm, "end": v(16.8, 21.82) * mm});
            skArc(sketch, "E12.4.0.1", {"start": v(13.82, 24.8) * mm, "mid": v(13.67, 24) * mm, "end": v(13.82, 23.2) * mm});
            skArc(sketch, "E12.4.0.2", {"start": v(16.8, 26.18) * mm, "mid": v(16, 26.32) * mm, "end": v(15.2, 26.18) * mm});
            skLineSegment(sketch, "E12.4.0.3", {"start": v(15.2, 26.18) * mm, "end": v(16.8, 26.18) * mm, "construction": true});
            skArc(sketch, "E12.4.0.4", {"start": v(18.18, 23.2) * mm, "mid": v(18.32, 24) * mm, "end": v(18.18, 24.8) * mm});
            skPoint(sketch, "E12.4.0.5", {"position": v(16, 24) * mm});
            skLineSegment(sketch, "E12.4.0.6", {"start": v(13.82, 24.8) * mm, "end": v(14.9, 24.8) * mm});
            skLineSegment(sketch, "E12.4.0.7", {"start": v(14.9, 23.2) * mm, "end": v(13.82, 23.2) * mm});
            skLineSegment(sketch, "E12.4.0.8", {"start": v(18.18, 23.2) * mm, "end": v(17.1, 23.2) * mm});
            skArc(sketch, "E12.4.0.9", {"start": v(17.1, 23.2) * mm, "mid": v(16.89, 23.11) * mm, "end": v(16.8, 22.9) * mm});
            skLineSegment(sketch, "E12.4.0.10", {"start": v(16, 24) * mm, "end": v(15.2, 26.18) * mm, "construction": true});
            skLineSegment(sketch, "E12.4.0.11", {"start": v(15.2, 21.82) * mm, "end": v(15.2, 22.9) * mm});
            skLineSegment(sketch, "E12.4.0.12", {"start": v(16.8, 22.9) * mm, "end": v(16.8, 21.82) * mm});
            skArc(sketch, "E12.4.0.13", {"start": v(15.2, 22.9) * mm, "mid": v(15.11, 23.11) * mm, "end": v(14.9, 23.2) * mm});
            skArc(sketch, "E12.4.0.14", {"start": v(14.9, 24.8) * mm, "mid": v(15.11, 24.89) * mm, "end": v(15.2, 25.1) * mm});
            skLineSegment(sketch, "E12.4.0.15", {"start": v(15.2, 25.1) * mm, "end": v(15.2, 26.18) * mm});
            skLineSegment(sketch, "E12.4.0.16", {"start": v(16.8, 24.8) * mm, "end": v(18.18, 24.8) * mm, "construction": true});
            skArc(sketch, "E12.4.0.17", {"start": v(16.8, 25.1) * mm, "mid": v(16.89, 24.89) * mm, "end": v(17.1, 24.8) * mm});
            skLineSegment(sketch, "E12.4.0.18", {"start": v(16.8, 26.18) * mm, "end": v(16.8, 24.8) * mm, "construction": true});
            skLineSegment(sketch, "E12.4.0.19", {"start": v(18.18, 24.8) * mm, "end": v(16, 24) * mm, "construction": true});
            skLineSegment(sketch, "E12.4.0.20", {"start": v(16.8, 26.18) * mm, "end": v(16.8, 25.1) * mm});
            skLineSegment(sketch, "E12.4.0.21", {"start": v(17.1, 24.8) * mm, "end": v(18.18, 24.8) * mm});
            skArc(sketch, "E12.4.1.0", {"start": v(15.2, 13.82) * mm, "mid": v(16, 13.67) * mm, "end": v(16.8, 13.82) * mm});
            skArc(sketch, "E12.4.1.1", {"start": v(13.82, 16.8) * mm, "mid": v(13.67, 16) * mm, "end": v(13.82, 15.2) * mm});
            skArc(sketch, "E12.4.1.2", {"start": v(16.8, 18.18) * mm, "mid": v(16, 18.32) * mm, "end": v(15.2, 18.18) * mm});
            skLineSegment(sketch, "E12.4.1.3", {"start": v(15.2, 18.18) * mm, "end": v(16.8, 18.18) * mm, "construction": true});
            skArc(sketch, "E12.4.1.4", {"start": v(18.18, 15.2) * mm, "mid": v(18.32, 16) * mm, "end": v(18.18, 16.8) * mm});
            skPoint(sketch, "E12.4.1.5", {"position": v(16, 16) * mm});
            skLineSegment(sketch, "E12.4.1.6", {"start": v(13.82, 16.8) * mm, "end": v(14.9, 16.8) * mm});
            skLineSegment(sketch, "E12.4.1.7", {"start": v(14.9, 15.2) * mm, "end": v(13.82, 15.2) * mm});
            skLineSegment(sketch, "E12.4.1.8", {"start": v(18.18, 15.2) * mm, "end": v(17.1, 15.2) * mm});
            skArc(sketch, "E12.4.1.9", {"start": v(17.1, 15.2) * mm, "mid": v(16.89, 15.11) * mm, "end": v(16.8, 14.9) * mm});
            skLineSegment(sketch, "E12.4.1.10", {"start": v(16, 16) * mm, "end": v(15.2, 18.18) * mm, "construction": true});
            skLineSegment(sketch, "E12.4.1.11", {"start": v(15.2, 13.82) * mm, "end": v(15.2, 14.9) * mm});
            skLineSegment(sketch, "E12.4.1.12", {"start": v(16.8, 14.9) * mm, "end": v(16.8, 13.82) * mm});
            skArc(sketch, "E12.4.1.13", {"start": v(15.2, 14.9) * mm, "mid": v(15.11, 15.11) * mm, "end": v(14.9, 15.2) * mm});
            skArc(sketch, "E12.4.1.14", {"start": v(14.9, 16.8) * mm, "mid": v(15.11, 16.89) * mm, "end": v(15.2, 17.1) * mm});
            skLineSegment(sketch, "E12.4.1.15", {"start": v(15.2, 17.1) * mm, "end": v(15.2, 18.18) * mm});
            skLineSegment(sketch, "E12.4.1.16", {"start": v(16.8, 16.8) * mm, "end": v(18.18, 16.8) * mm, "construction": true});
            skArc(sketch, "E12.4.1.17", {"start": v(16.8, 17.1) * mm, "mid": v(16.89, 16.89) * mm, "end": v(17.1, 16.8) * mm});
            skLineSegment(sketch, "E12.4.1.18", {"start": v(16.8, 18.18) * mm, "end": v(16.8, 16.8) * mm, "construction": true});
            skLineSegment(sketch, "E12.4.1.19", {"start": v(18.18, 16.8) * mm, "end": v(16, 16) * mm, "construction": true});
            skLineSegment(sketch, "E12.4.1.20", {"start": v(16.8, 18.18) * mm, "end": v(16.8, 17.1) * mm});
            skLineSegment(sketch, "E12.4.1.21", {"start": v(17.1, 16.8) * mm, "end": v(18.18, 16.8) * mm});
            skArc(sketch, "E12.4.2.0", {"start": v(15.2, 5.82) * mm, "mid": v(16, 5.67) * mm, "end": v(16.8, 5.82) * mm});
            skArc(sketch, "E12.4.2.1", {"start": v(13.82, 8.8) * mm, "mid": v(13.67, 8) * mm, "end": v(13.82, 7.2) * mm});
            skArc(sketch, "E12.4.2.2", {"start": v(16.8, 10.18) * mm, "mid": v(16, 10.32) * mm, "end": v(15.2, 10.18) * mm});
            skLineSegment(sketch, "E12.4.2.3", {"start": v(15.2, 10.18) * mm, "end": v(16.8, 10.18) * mm, "construction": true});
            skArc(sketch, "E12.4.2.4", {"start": v(18.18, 7.2) * mm, "mid": v(18.32, 8) * mm, "end": v(18.18, 8.8) * mm});
            skPoint(sketch, "E12.4.2.5", {"position": v(16, 8) * mm});
            skLineSegment(sketch, "E12.4.2.6", {"start": v(13.82, 8.8) * mm, "end": v(14.9, 8.8) * mm});
            skLineSegment(sketch, "E12.4.2.7", {"start": v(14.9, 7.2) * mm, "end": v(13.82, 7.2) * mm});
            skLineSegment(sketch, "E12.4.2.8", {"start": v(18.18, 7.2) * mm, "end": v(17.1, 7.2) * mm});
            skArc(sketch, "E12.4.2.9", {"start": v(17.1, 7.2) * mm, "mid": v(16.89, 7.11) * mm, "end": v(16.8, 6.9) * mm});
            skLineSegment(sketch, "E12.4.2.10", {"start": v(16, 8) * mm, "end": v(15.2, 10.18) * mm, "construction": true});
            skLineSegment(sketch, "E12.4.2.11", {"start": v(15.2, 5.82) * mm, "end": v(15.2, 6.9) * mm});
            skLineSegment(sketch, "E12.4.2.12", {"start": v(16.8, 6.9) * mm, "end": v(16.8, 5.82) * mm});
            skArc(sketch, "E12.4.2.13", {"start": v(15.2, 6.9) * mm, "mid": v(15.11, 7.11) * mm, "end": v(14.9, 7.2) * mm});
            skArc(sketch, "E12.4.2.14", {"start": v(14.9, 8.8) * mm, "mid": v(15.11, 8.89) * mm, "end": v(15.2, 9.1) * mm});
            skLineSegment(sketch, "E12.4.2.15", {"start": v(15.2, 9.1) * mm, "end": v(15.2, 10.18) * mm});
            skLineSegment(sketch, "E12.4.2.16", {"start": v(16.8, 8.8) * mm, "end": v(18.18, 8.8) * mm, "construction": true});
            skArc(sketch, "E12.4.2.17", {"start": v(16.8, 9.1) * mm, "mid": v(16.89, 8.89) * mm, "end": v(17.1, 8.8) * mm});
            skLineSegment(sketch, "E12.4.2.18", {"start": v(16.8, 10.18) * mm, "end": v(16.8, 8.8) * mm, "construction": true});
            skLineSegment(sketch, "E12.4.2.19", {"start": v(18.18, 8.8) * mm, "end": v(16, 8) * mm, "construction": true});
            skLineSegment(sketch, "E12.4.2.20", {"start": v(16.8, 10.18) * mm, "end": v(16.8, 9.1) * mm});
            skLineSegment(sketch, "E12.4.2.21", {"start": v(17.1, 8.8) * mm, "end": v(18.18, 8.8) * mm});
            skArc(sketch, "E12.4.3.0", {"start": v(15.2, -2.18) * mm, "mid": v(16, -2.33) * mm, "end": v(16.8, -2.18) * mm});
            skArc(sketch, "E12.4.3.1", {"start": v(13.82, 0.8) * mm, "mid": v(13.67, 0) * mm, "end": v(13.82, -0.8) * mm});
            skArc(sketch, "E12.4.3.2", {"start": v(16.8, 2.18) * mm, "mid": v(16, 2.32) * mm, "end": v(15.2, 2.18) * mm});
            skLineSegment(sketch, "E12.4.3.3", {"start": v(15.2, 2.18) * mm, "end": v(16.8, 2.18) * mm, "construction": true});
            skArc(sketch, "E12.4.3.4", {"start": v(18.18, -0.8) * mm, "mid": v(18.32, 0) * mm, "end": v(18.18, 0.8) * mm});
            skPoint(sketch, "E12.4.3.5", {"position": v(16, 0) * mm});
            skLineSegment(sketch, "E12.4.3.6", {"start": v(13.82, 0.8) * mm, "end": v(14.9, 0.8) * mm});
            skLineSegment(sketch, "E12.4.3.7", {"start": v(14.9, -0.8) * mm, "end": v(13.82, -0.8) * mm});
            skLineSegment(sketch, "E12.4.3.8", {"start": v(18.18, -0.8) * mm, "end": v(17.1, -0.8) * mm});
            skArc(sketch, "E12.4.3.9", {"start": v(17.1, -0.8) * mm, "mid": v(16.89, -0.89) * mm, "end": v(16.8, -1.1) * mm});
            skLineSegment(sketch, "E12.4.3.10", {"start": v(16, 0) * mm, "end": v(15.2, 2.18) * mm, "construction": true});
            skLineSegment(sketch, "E12.4.3.11", {"start": v(15.2, -2.18) * mm, "end": v(15.2, -1.1) * mm});
            skLineSegment(sketch, "E12.4.3.12", {"start": v(16.8, -1.1) * mm, "end": v(16.8, -2.18) * mm});
            skArc(sketch, "E12.4.3.13", {"start": v(15.2, -1.1) * mm, "mid": v(15.11, -0.89) * mm, "end": v(14.9, -0.8) * mm});
            skArc(sketch, "E12.4.3.14", {"start": v(14.9, 0.8) * mm, "mid": v(15.11, 0.89) * mm, "end": v(15.2, 1.1) * mm});
            skLineSegment(sketch, "E12.4.3.15", {"start": v(15.2, 1.1) * mm, "end": v(15.2, 2.18) * mm});
            skLineSegment(sketch, "E12.4.3.16", {"start": v(16.8, 0.8) * mm, "end": v(18.18, 0.8) * mm, "construction": true});
            skArc(sketch, "E12.4.3.17", {"start": v(16.8, 1.1) * mm, "mid": v(16.89, 0.89) * mm, "end": v(17.1, 0.8) * mm});
            skLineSegment(sketch, "E12.4.3.18", {"start": v(16.8, 2.18) * mm, "end": v(16.8, 0.8) * mm, "construction": true});
            skLineSegment(sketch, "E12.4.3.19", {"start": v(18.18, 0.8) * mm, "end": v(16, 0) * mm, "construction": true});
            skLineSegment(sketch, "E12.4.3.20", {"start": v(16.8, 2.18) * mm, "end": v(16.8, 1.1) * mm});
            skLineSegment(sketch, "E12.4.3.21", {"start": v(17.1, 0.8) * mm, "end": v(18.18, 0.8) * mm});
            skArc(sketch, "E12.4.4.0", {"start": v(15.2, -10.18) * mm, "mid": v(16, -10.33) * mm, "end": v(16.8, -10.18) * mm});
            skArc(sketch, "E12.4.4.1", {"start": v(13.82, -7.2) * mm, "mid": v(13.68, -8) * mm, "end": v(13.82, -8.8) * mm});
            skArc(sketch, "E12.4.4.2", {"start": v(16.8, -5.82) * mm, "mid": v(16, -5.68) * mm, "end": v(15.2, -5.82) * mm});
            skLineSegment(sketch, "E12.4.4.3", {"start": v(15.2, -5.82) * mm, "end": v(16.8, -5.82) * mm, "construction": true});
            skArc(sketch, "E12.4.4.4", {"start": v(18.18, -8.8) * mm, "mid": v(18.33, -8) * mm, "end": v(18.18, -7.2) * mm});
            skPoint(sketch, "E12.4.4.5", {"position": v(16, -8) * mm});
            skLineSegment(sketch, "E12.4.4.6", {"start": v(13.82, -7.2) * mm, "end": v(14.9, -7.2) * mm});
            skLineSegment(sketch, "E12.4.4.7", {"start": v(14.9, -8.8) * mm, "end": v(13.82, -8.8) * mm});
            skLineSegment(sketch, "E12.4.4.8", {"start": v(18.18, -8.8) * mm, "end": v(17.1, -8.8) * mm});
            skArc(sketch, "E12.4.4.9", {"start": v(17.1, -8.8) * mm, "mid": v(16.89, -8.89) * mm, "end": v(16.8, -9.1) * mm});
            skLineSegment(sketch, "E12.4.4.10", {"start": v(16, -8) * mm, "end": v(15.2, -5.82) * mm, "construction": true});
            skLineSegment(sketch, "E12.4.4.11", {"start": v(15.2, -10.18) * mm, "end": v(15.2, -9.1) * mm});
            skLineSegment(sketch, "E12.4.4.12", {"start": v(16.8, -9.1) * mm, "end": v(16.8, -10.18) * mm});
            skArc(sketch, "E12.4.4.13", {"start": v(15.2, -9.1) * mm, "mid": v(15.11, -8.89) * mm, "end": v(14.9, -8.8) * mm});
            skArc(sketch, "E12.4.4.14", {"start": v(14.9, -7.2) * mm, "mid": v(15.11, -7.11) * mm, "end": v(15.2, -6.9) * mm});
            skLineSegment(sketch, "E12.4.4.15", {"start": v(15.2, -6.9) * mm, "end": v(15.2, -5.82) * mm});
            skLineSegment(sketch, "E12.4.4.16", {"start": v(16.8, -7.2) * mm, "end": v(18.18, -7.2) * mm, "construction": true});
            skArc(sketch, "E12.4.4.17", {"start": v(16.8, -6.9) * mm, "mid": v(16.89, -7.11) * mm, "end": v(17.1, -7.2) * mm});
            skLineSegment(sketch, "E12.4.4.18", {"start": v(16.8, -5.82) * mm, "end": v(16.8, -7.2) * mm, "construction": true});
            skLineSegment(sketch, "E12.4.4.19", {"start": v(18.18, -7.2) * mm, "end": v(16, -8) * mm, "construction": true});
            skLineSegment(sketch, "E12.4.4.20", {"start": v(16.8, -5.82) * mm, "end": v(16.8, -6.9) * mm});
            skLineSegment(sketch, "E12.4.4.21", {"start": v(17.1, -7.2) * mm, "end": v(18.18, -7.2) * mm});
            skArc(sketch, "E12.4.5.0", {"start": v(15.2, -18.18) * mm, "mid": v(16, -18.33) * mm, "end": v(16.8, -18.18) * mm});
            skArc(sketch, "E12.4.5.1", {"start": v(13.82, -15.2) * mm, "mid": v(13.68, -16) * mm, "end": v(13.82, -16.8) * mm});
            skArc(sketch, "E12.4.5.2", {"start": v(16.8, -13.82) * mm, "mid": v(16, -13.68) * mm, "end": v(15.2, -13.82) * mm});
            skLineSegment(sketch, "E12.4.5.3", {"start": v(15.2, -13.82) * mm, "end": v(16.8, -13.82) * mm, "construction": true});
            skArc(sketch, "E12.4.5.4", {"start": v(18.18, -16.8) * mm, "mid": v(18.33, -16) * mm, "end": v(18.18, -15.2) * mm});
            skPoint(sketch, "E12.4.5.5", {"position": v(16, -16) * mm});
            skLineSegment(sketch, "E12.4.5.6", {"start": v(13.82, -15.2) * mm, "end": v(14.9, -15.2) * mm});
            skLineSegment(sketch, "E12.4.5.7", {"start": v(14.9, -16.8) * mm, "end": v(13.82, -16.8) * mm});
            skLineSegment(sketch, "E12.4.5.8", {"start": v(18.18, -16.8) * mm, "end": v(17.1, -16.8) * mm});
            skArc(sketch, "E12.4.5.9", {"start": v(17.1, -16.8) * mm, "mid": v(16.89, -16.89) * mm, "end": v(16.8, -17.1) * mm});
            skLineSegment(sketch, "E12.4.5.10", {"start": v(16, -16) * mm, "end": v(15.2, -13.82) * mm, "construction": true});
            skLineSegment(sketch, "E12.4.5.11", {"start": v(15.2, -18.18) * mm, "end": v(15.2, -17.1) * mm});
            skLineSegment(sketch, "E12.4.5.12", {"start": v(16.8, -17.1) * mm, "end": v(16.8, -18.18) * mm});
            skArc(sketch, "E12.4.5.13", {"start": v(15.2, -17.1) * mm, "mid": v(15.11, -16.89) * mm, "end": v(14.9, -16.8) * mm});
            skArc(sketch, "E12.4.5.14", {"start": v(14.9, -15.2) * mm, "mid": v(15.11, -15.11) * mm, "end": v(15.2, -14.9) * mm});
            skLineSegment(sketch, "E12.4.5.15", {"start": v(15.2, -14.9) * mm, "end": v(15.2, -13.82) * mm});
            skLineSegment(sketch, "E12.4.5.16", {"start": v(16.8, -15.2) * mm, "end": v(18.18, -15.2) * mm, "construction": true});
            skArc(sketch, "E12.4.5.17", {"start": v(16.8, -14.9) * mm, "mid": v(16.89, -15.11) * mm, "end": v(17.1, -15.2) * mm});
            skLineSegment(sketch, "E12.4.5.18", {"start": v(16.8, -13.82) * mm, "end": v(16.8, -15.2) * mm, "construction": true});
            skLineSegment(sketch, "E12.4.5.19", {"start": v(18.18, -15.2) * mm, "end": v(16, -16) * mm, "construction": true});
            skLineSegment(sketch, "E12.4.5.20", {"start": v(16.8, -13.82) * mm, "end": v(16.8, -14.9) * mm});
            skLineSegment(sketch, "E12.4.5.21", {"start": v(17.1, -15.2) * mm, "end": v(18.18, -15.2) * mm});
            skArc(sketch, "E12.4.6.0", {"start": v(15.2, -26.18) * mm, "mid": v(16, -26.33) * mm, "end": v(16.8, -26.18) * mm});
            skArc(sketch, "E12.4.6.1", {"start": v(13.82, -23.2) * mm, "mid": v(13.68, -24) * mm, "end": v(13.82, -24.8) * mm});
            skArc(sketch, "E12.4.6.2", {"start": v(16.8, -21.82) * mm, "mid": v(16, -21.68) * mm, "end": v(15.2, -21.82) * mm});
            skLineSegment(sketch, "E12.4.6.3", {"start": v(15.2, -21.82) * mm, "end": v(16.8, -21.82) * mm, "construction": true});
            skArc(sketch, "E12.4.6.4", {"start": v(18.18, -24.8) * mm, "mid": v(18.33, -24) * mm, "end": v(18.18, -23.2) * mm});
            skPoint(sketch, "E12.4.6.5", {"position": v(16, -24) * mm});
            skLineSegment(sketch, "E12.4.6.6", {"start": v(13.82, -23.2) * mm, "end": v(14.9, -23.2) * mm});
            skLineSegment(sketch, "E12.4.6.7", {"start": v(14.9, -24.8) * mm, "end": v(13.82, -24.8) * mm});
            skLineSegment(sketch, "E12.4.6.8", {"start": v(18.18, -24.8) * mm, "end": v(17.1, -24.8) * mm});
            skArc(sketch, "E12.4.6.9", {"start": v(17.1, -24.8) * mm, "mid": v(16.89, -24.89) * mm, "end": v(16.8, -25.1) * mm});
            skLineSegment(sketch, "E12.4.6.10", {"start": v(16, -24) * mm, "end": v(15.2, -21.82) * mm, "construction": true});
            skLineSegment(sketch, "E12.4.6.11", {"start": v(15.2, -26.18) * mm, "end": v(15.2, -25.1) * mm});
            skLineSegment(sketch, "E12.4.6.12", {"start": v(16.8, -25.1) * mm, "end": v(16.8, -26.18) * mm});
            skArc(sketch, "E12.4.6.13", {"start": v(15.2, -25.1) * mm, "mid": v(15.11, -24.89) * mm, "end": v(14.9, -24.8) * mm});
            skArc(sketch, "E12.4.6.14", {"start": v(14.9, -23.2) * mm, "mid": v(15.11, -23.11) * mm, "end": v(15.2, -22.9) * mm});
            skLineSegment(sketch, "E12.4.6.15", {"start": v(15.2, -22.9) * mm, "end": v(15.2, -21.82) * mm});
            skLineSegment(sketch, "E12.4.6.16", {"start": v(16.8, -23.2) * mm, "end": v(18.18, -23.2) * mm, "construction": true});
            skArc(sketch, "E12.4.6.17", {"start": v(16.8, -22.9) * mm, "mid": v(16.89, -23.11) * mm, "end": v(17.1, -23.2) * mm});
            skLineSegment(sketch, "E12.4.6.18", {"start": v(16.8, -21.82) * mm, "end": v(16.8, -23.2) * mm, "construction": true});
            skLineSegment(sketch, "E12.4.6.19", {"start": v(18.18, -23.2) * mm, "end": v(16, -24) * mm, "construction": true});
            skLineSegment(sketch, "E12.4.6.20", {"start": v(16.8, -21.82) * mm, "end": v(16.8, -22.9) * mm});
            skLineSegment(sketch, "E12.4.6.21", {"start": v(17.1, -23.2) * mm, "end": v(18.18, -23.2) * mm});
            skArc(sketch, "E12.4.7.0", {"start": v(15.2, -34.18) * mm, "mid": v(16, -34.33) * mm, "end": v(16.8, -34.18) * mm});
            skArc(sketch, "E12.4.7.1", {"start": v(13.82, -31.2) * mm, "mid": v(13.68, -32) * mm, "end": v(13.82, -32.8) * mm});
            skArc(sketch, "E12.4.7.2", {"start": v(16.8, -29.82) * mm, "mid": v(16, -29.68) * mm, "end": v(15.2, -29.82) * mm});
            skLineSegment(sketch, "E12.4.7.3", {"start": v(15.2, -29.82) * mm, "end": v(16.8, -29.82) * mm, "construction": true});
            skArc(sketch, "E12.4.7.4", {"start": v(18.18, -32.8) * mm, "mid": v(18.33, -32) * mm, "end": v(18.18, -31.2) * mm});
            skPoint(sketch, "E12.4.7.5", {"position": v(16, -32) * mm});
            skLineSegment(sketch, "E12.4.7.6", {"start": v(13.82, -31.2) * mm, "end": v(14.9, -31.2) * mm});
            skLineSegment(sketch, "E12.4.7.7", {"start": v(14.9, -32.8) * mm, "end": v(13.82, -32.8) * mm});
            skLineSegment(sketch, "E12.4.7.8", {"start": v(18.18, -32.8) * mm, "end": v(17.1, -32.8) * mm});
            skArc(sketch, "E12.4.7.9", {"start": v(17.1, -32.8) * mm, "mid": v(16.89, -32.89) * mm, "end": v(16.8, -33.1) * mm});
            skLineSegment(sketch, "E12.4.7.10", {"start": v(16, -32) * mm, "end": v(15.2, -29.82) * mm, "construction": true});
            skLineSegment(sketch, "E12.4.7.11", {"start": v(15.2, -34.18) * mm, "end": v(15.2, -33.1) * mm});
            skLineSegment(sketch, "E12.4.7.12", {"start": v(16.8, -33.1) * mm, "end": v(16.8, -34.18) * mm});
            skArc(sketch, "E12.4.7.13", {"start": v(15.2, -33.1) * mm, "mid": v(15.11, -32.89) * mm, "end": v(14.9, -32.8) * mm});
            skArc(sketch, "E12.4.7.14", {"start": v(14.9, -31.2) * mm, "mid": v(15.11, -31.11) * mm, "end": v(15.2, -30.9) * mm});
            skLineSegment(sketch, "E12.4.7.15", {"start": v(15.2, -30.9) * mm, "end": v(15.2, -29.82) * mm});
            skLineSegment(sketch, "E12.4.7.16", {"start": v(16.8, -31.2) * mm, "end": v(18.18, -31.2) * mm, "construction": true});
            skArc(sketch, "E12.4.7.17", {"start": v(16.8, -30.9) * mm, "mid": v(16.89, -31.11) * mm, "end": v(17.1, -31.2) * mm});
            skLineSegment(sketch, "E12.4.7.18", {"start": v(16.8, -29.82) * mm, "end": v(16.8, -31.2) * mm, "construction": true});
            skLineSegment(sketch, "E12.4.7.19", {"start": v(18.18, -31.2) * mm, "end": v(16, -32) * mm, "construction": true});
            skLineSegment(sketch, "E12.4.7.20", {"start": v(16.8, -29.82) * mm, "end": v(16.8, -30.9) * mm});
            skLineSegment(sketch, "E12.4.7.21", {"start": v(17.1, -31.2) * mm, "end": v(18.18, -31.2) * mm});
            skLineSegment(sketch, "E12.direction1", {"start": v(-16.8, 21.82) * mm, "end": v(-8.8, 21.82) * mm, "construction": true});
            skLineSegment(sketch, "E12.direction2", {"start": v(-16.8, 21.82) * mm, "end": v(-16.8, 13.82) * mm, "construction": true});
            skSolve(sketch);
        }
        {
            var Q0;
            Q0=makeQuery(id+"F0.imprint","IMPRINT",FACE,{"disambiguationData":[TD([[makeQuery(id+"F0.imprint","IMPRINT",EDGE,{"derivedFrom":sQuery(id+"F0.wireOp",EDGE,"E2")}),1.0]])]});
            var Q1;
            Q1=makeQuery(id+"F0.imprint","IMPRINT",FACE,{"disambiguationData":[TD([[makeQuery(id+"F0.imprint","IMPRINT",EDGE,{"derivedFrom":sQuery(id+"F0.wireOp",EDGE,"2cf9ed89-b0f7-4121-92e4-3c978841a4d5.2.1.0")}),1.0]])]});
            var Q2;
            Q2=makeQuery(id+"F0.imprint","IMPRINT",FACE,{"disambiguationData":[TD([[makeQuery(id+"F0.imprint","IMPRINT",EDGE,{"derivedFrom":sQuery(id+"F0.wireOp",EDGE,"2cf9ed89-b0f7-4121-92e4-3c978841a4d5.2.2.0")}),1.0]])]});
            var Q3;
            Q3=makeQuery(id+"F0.imprint","IMPRINT",FACE,{"disambiguationData":[TD([[makeQuery(id+"F0.imprint","IMPRINT",EDGE,{"derivedFrom":sQuery(id+"F0.wireOp",EDGE,"2cf9ed89-b0f7-4121-92e4-3c978841a4d5.2.4.0")}),1.0]])]});
            var Q4;
            Q4=makeQuery(id+"F0.imprint","IMPRINT",FACE,{"disambiguationData":[TD([[makeQuery(id+"F0.imprint","IMPRINT",EDGE,{"derivedFrom":sQuery(id+"F0.wireOp",EDGE,"d1a7959e-7c20-4f30-b70b-c3a01a31882a.0.2.5")}),1.0]])]});
            var Q5;
            Q5=makeQuery(id+"F0.imprint","IMPRINT",FACE,{"disambiguationData":[TD([[makeQuery(id+"F0.imprint","IMPRINT",EDGE,{"derivedFrom":sQuery(id+"F0.wireOp",EDGE,"2cf9ed89-b0f7-4121-92e4-3c978841a4d5.2.3.0")}),1.0]])]});
            var Q6;
            Q6=makeQuery(id+"F0.imprint","IMPRINT",FACE,{"disambiguationData":[TD([[makeQuery(id+"F0.imprint","IMPRINT",EDGE,{"derivedFrom":sQuery(id+"F0.wireOp",EDGE,"2cf9ed89-b0f7-4121-92e4-3c978841a4d5.0.4.0")}),1.0]])]});
            var Q7;
            Q7=makeQuery(id+"F0.imprint","IMPRINT",FACE,{"disambiguationData":[TD([[makeQuery(id+"F0.imprint","IMPRINT",EDGE,{"derivedFrom":sQuery(id+"F0.wireOp",EDGE,"2cf9ed89-b0f7-4121-92e4-3c978841a4d5.1.4.0")}),1.0]])]});
            var Q8;
            Q8=makeQuery(id+"F0.imprint","IMPRINT",FACE,{"disambiguationData":[TD([[makeQuery(id+"F0.imprint","IMPRINT",EDGE,{"derivedFrom":sQuery(id+"F0.wireOp",EDGE,"2cf9ed89-b0f7-4121-92e4-3c978841a4d5.1.3.0")}),1.0]])]});
            var Q9;
            Q9=makeQuery(id+"F0.imprint","IMPRINT",FACE,{"disambiguationData":[TD([[makeQuery(id+"F0.imprint","IMPRINT",EDGE,{"derivedFrom":sQuery(id+"F0.wireOp",EDGE,"2cf9ed89-b0f7-4121-92e4-3c978841a4d5.1.2.0")}),1.0]])]});
            var Q10;
            Q10=makeQuery(id+"F0.imprint","IMPRINT",FACE,{"disambiguationData":[TD([[makeQuery(id+"F0.imprint","IMPRINT",EDGE,{"derivedFrom":sQuery(id+"F0.wireOp",EDGE,"2cf9ed89-b0f7-4121-92e4-3c978841a4d5.0.2.0")}),1.0]])]});
            var Q11;
            Q11=makeQuery(id+"F0.imprint","IMPRINT",FACE,{"disambiguationData":[TD([[makeQuery(id+"F0.imprint","IMPRINT",EDGE,{"derivedFrom":sQuery(id+"F0.wireOp",EDGE,"9defd455-20d1-4dd0-b371-d9f08b347be7.0.3.2")}),1.0]])]});
            var Q12;
            Q12=makeQuery(id+"F0.imprint","IMPRINT",FACE,{"disambiguationData":[TD([[makeQuery(id+"F0.imprint","IMPRINT",EDGE,{"derivedFrom":sQuery(id+"F0.wireOp",EDGE,"acadd5ce-ef53-486c-b287-4d7b5f0021c8.0.4.2")}),1.0]])]});
            var Q13;
            Q13=makeQuery(id+"F0.imprint","IMPRINT",FACE,{"disambiguationData":[TD([[makeQuery(id+"F0.imprint","IMPRINT",EDGE,{"derivedFrom":sQuery(id+"F0.wireOp",EDGE,"acadd5ce-ef53-486c-b287-4d7b5f0021c8.0.4.3")}),1.0]])]});
            var Q14;
            Q14=makeQuery(id+"F0.imprint","IMPRINT",FACE,{"disambiguationData":[TD([[makeQuery(id+"F0.imprint","IMPRINT",EDGE,{"derivedFrom":sQuery(id+"F0.wireOp",EDGE,"9defd455-20d1-4dd0-b371-d9f08b347be7.0.3.4")}),1.0]])]});
            var Q15;
            Q15=makeQuery(id+"F0.imprint","IMPRINT",FACE,{"disambiguationData":[TD([[makeQuery(id+"F0.imprint","IMPRINT",EDGE,{"derivedFrom":sQuery(id+"F0.wireOp",EDGE,"acadd5ce-ef53-486c-b287-4d7b5f0021c8.0.4.4")}),1.0]])]});
            var Q16;
            Q16=makeQuery(id+"F0.imprint","IMPRINT",FACE,{"disambiguationData":[TD([[makeQuery(id+"F0.imprint","IMPRINT",EDGE,{"derivedFrom":sQuery(id+"F0.wireOp",EDGE,"2cf9ed89-b0f7-4121-92e4-3c978841a4d5.0.3.0")}),1.0]])]});
            var Q17;
            Q17=makeQuery(id+"F0.imprint","IMPRINT",FACE,{"disambiguationData":[TD([[makeQuery(id+"F0.imprint","IMPRINT",EDGE,{"derivedFrom":sQuery(id+"F0.wireOp",EDGE,"9defd455-20d1-4dd0-b371-d9f08b347be7.0.3.3")}),1.0]])]});
            extrude(context, id + "F1", {"entities" : qUnion([Q0, Q1, Q2, Q3, Q4, Q5, Q6, Q7, Q8, Q9, Q10, Q11, Q12, Q13, Q14, Q15, Q16, Q17]), "depth" : 3 * mm, "offsetDistance" : 25 * mm});
        }
        {
            var Q0;
            Q0=qCreatedBy(makeId("Top.planeOp"),FACE);
            var sketch = newSketch(context, id + "F2", { "sketchPlane" : qUnion([Q0])});
            skCircle(sketch, "E13", {"center": v(0, 0) * mm, "radius": 14 * mm});
            skLineSegment(sketch, "E14", {"start": v(11.98, 7.25) * mm, "end": v(17.5, 7.25) * mm});
            skLineSegment(sketch, "E15", {"start": v(17.5, 7.25) * mm, "end": v(17.5, -7.25) * mm});
            skLineSegment(sketch, "E16", {"start": v(17.5, -7.25) * mm, "end": v(11.98, -7.25) * mm});
            skLineSegment(sketch, "E17", {"start": v(-3.5, 13.56) * mm, "end": v(-3.5, 17.06) * mm});
            skLineSegment(sketch, "E18", {"start": v(-3.5, 17.06) * mm, "end": v(3.5, 17.06) * mm, "construction": true});
            skLineSegment(sketch, "E19", {"start": v(3.5, 17.06) * mm, "end": v(3.5, 13.56) * mm});
            skLineSegment(sketch, "E20", {"start": v(-3.5, -13.56) * mm, "end": v(-3.5, -17.06) * mm});
            skLineSegment(sketch, "E21", {"start": v(-3.5, -17.06) * mm, "end": v(3.5, -17.06) * mm, "construction": true});
            skLineSegment(sketch, "E22", {"start": v(3.5, -17.06) * mm, "end": v(3.5, -13.56) * mm});
            skLineSegment(sketch, "E23", {"start": v(-40.2, 0) * mm, "end": v(27.14, 0) * mm, "construction": true});
            skCircle(sketch, "E24", {"center": v(0, -17.06) * mm, "radius": 2.1 * mm});
            skCircle(sketch, "E25", {"center": v(0, 17.06) * mm, "radius": 2.1 * mm});
            skArc(sketch, "E26", {"start": v(3.5, 17.06) * mm, "mid": v(0, 20.56) * mm, "end": v(-3.5, 17.06) * mm});
            skArc(sketch, "E27", {"start": v(-3.5, -17.06) * mm, "mid": v(0, -20.56) * mm, "end": v(3.5, -17.06) * mm});
            skCircle(sketch, "E28", {"center": v(-8, 0) * mm, "radius": 4.5 * mm});
            skLineSegment(sketch, "E29", {"start": v(-3.5, 13.56) * mm, "end": v(3.5, 13.56) * mm, "construction": true});
            skSolve(sketch);
        }
    });
